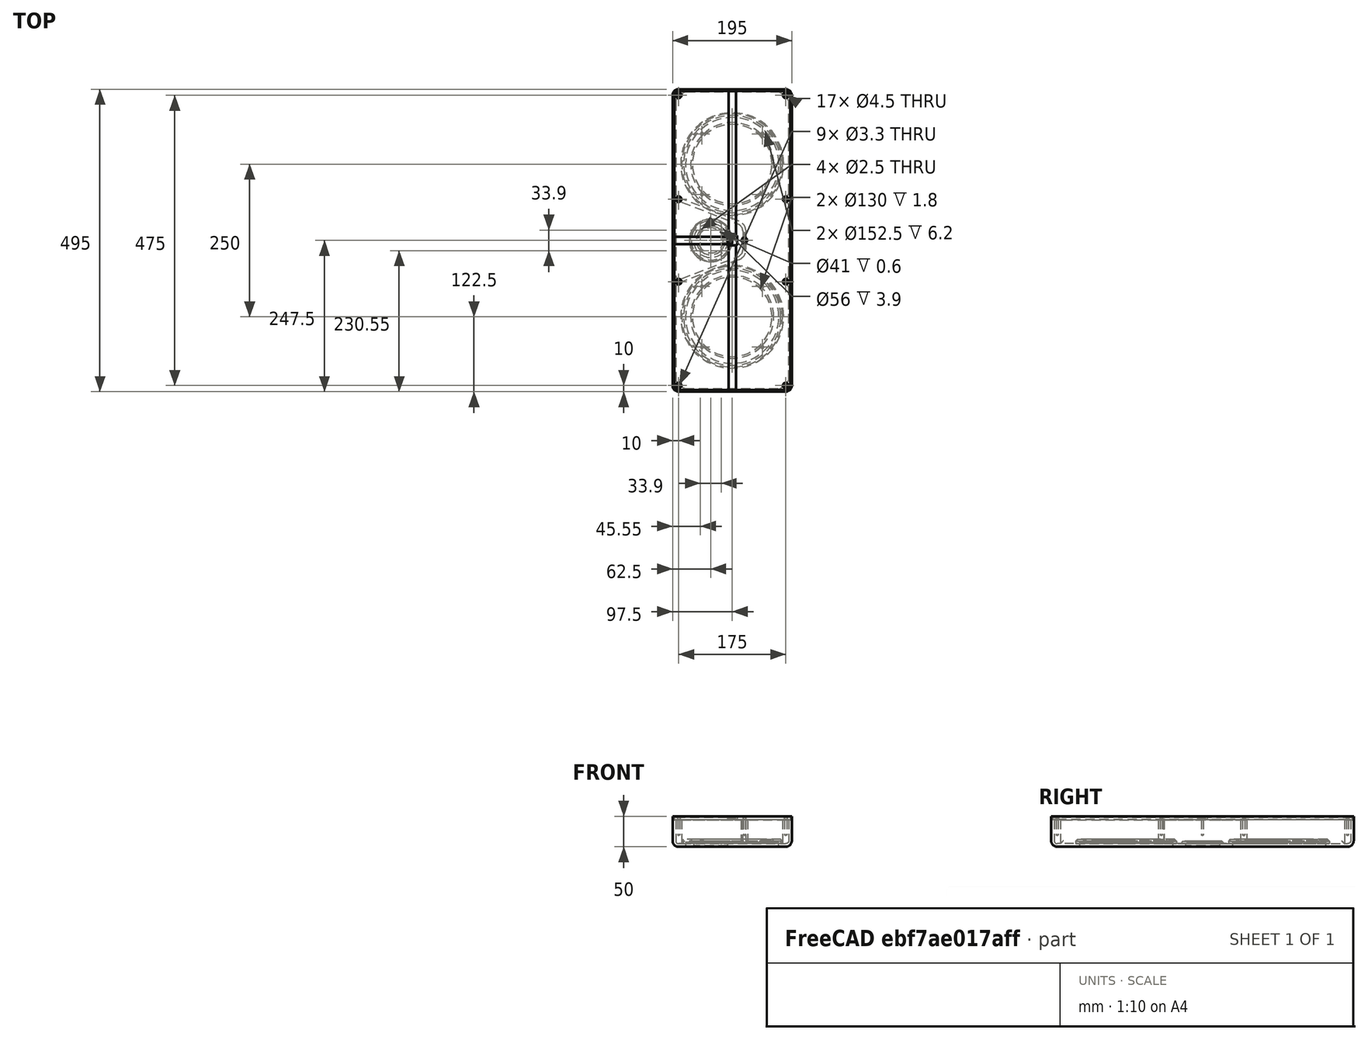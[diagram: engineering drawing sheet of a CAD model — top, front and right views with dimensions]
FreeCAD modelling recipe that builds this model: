
FCSTD DOCUMENT  (FreeCAD 1.1R20260325 (Git shallow))
Label: wallspeakers prototype v6.2
License: All rights reserved
LicenseURL: http://en.wikipedia.org/wiki/All_rights_reserved
objects: TechDraw::DrawViewDimension×43, Sketcher::SketchObject×20, TechDraw::DrawViewAnnotation×7, PartDesign::Pocket×7, PartDesign::Pad×6, TechDraw::DrawProjGroupItem×5, TechDraw::DrawSVGTemplate×4, TechDraw::DrawPage×4, PartDesign::Hole×4, PartDesign::Chamfer×4, App::Point×2, PartDesign::Fillet×2, TechDraw::DrawViewImage×2, Part::Feature×2, PartDesign::Body×2, App::VarSet×1, PartDesign::Thickness×1, App::DocumentObjectGroup×1, Mesh::Feature×1
note: 185 computed .brp shape members not serialized (recipe doc carries the construction recipe); baked Part::Feature solids carry a one-line shape summary decoded from their .brp

FEATURE [Sketcher::SketchObject] Sketch002  label="base geometry"
  ArcFitTolerance = 1e-06
  AttachmentSupport = -> [XY_Plane]
  ExternalTypes = [0]
  FullyConstrained = true
  MakeInternals = false
  MapMode = 5
  _ExternalGeoVersion = 0
  expr: Constraints[3] = <<v>>.bmr_offset
  expr: Constraints[4] = <<v>>.woofer_offset
  expr: Constraints[5] = <<v>>.woofer_offset
  expr: Constraints[6] = <<v>>.ext_height / 2
  expr: Constraints[7] = <<v>>.ext_width / 2
  sketch-geometry (7):
    g0: GeomPoint [constr] X=-97.5 Y=247.5 Z=0
    g1: GeomPoint [constr] X=97.5 Y=247.5 Z=0
    g2: GeomPoint [constr] X=97.5 Y=-247.5 Z=0
    g3: GeomPoint [constr] X=-97.5 Y=-247.5 Z=0
    g4: GeomPoint [constr] X=-35 Y=0 Z=0
    g5: GeomPoint [constr] X=0 Y=125 Z=0
    g6: GeomPoint [constr] X=0 Y=-125 Z=0
  constraints (11):
    c: PointOnObject(g4,g-1)
    c: PointOnObject(g5,g-2)
    c: PointOnObject(g6,g-2)
    c: DistanceX(g4,g-1) = 35
    c: DistanceY(g-1,g5) = 125
    c: DistanceY(g6,g-1) = 125
    c: DistanceY(g-1,g1) = 247.5
    c: DistanceX(g-1,g1) = 97.5
    c: Symmetric(g0,g1,g-2)
    c: Symmetric(g1,g2,g-1)
    c: Symmetric(g3,g2,g-2)
FEATURE [Sketcher::SketchObject] Sketch  label="back panel screw hole geometry"
  ArcFitTolerance = 1e-06
  AttachmentSupport = -> [Sketch002]
  ExternalTypes = [0]
  FullyConstrained = true
  MakeInternals = false
  MapMode = 2
  _ExternalGeoVersion = 0
  expr: Constraints[11] = <<v>>.bmr_enc_offset
  expr: Constraints[1] = <<v>>.ext_height / 2 - <<v>>.screw_inset
  expr: Constraints[2] = <<v>>.ext_width / 2 - <<v>>.screw_inset
  expr: Constraints[8] = <<v>>.ext_width / 2 - <<v>>.screw_inset
  expr: Constraints[9] = <<v>>.bmr_enc_base
  sketch-geometry (9):
    g0: GeomPoint [constr] X=-87.5 Y=237.5 Z=0
    g1: GeomPoint [constr] X=87.5 Y=237.5 Z=0
    g2: GeomPoint [constr] X=87.5 Y=-237.5 Z=0
    g3: GeomPoint [constr] X=-87.5 Y=-237.5 Z=0
    g4: GeomPoint [constr] X=-87.5 Y=-67.5 Z=0
    g5: GeomPoint [constr] X=-87.5 Y=67.5 Z=0
    g6: GeomPoint [constr] X=87.5 Y=67.5 Z=0
    g7: GeomPoint [constr] X=87.5 Y=-67.5 Z=0
    g8: GeomPoint [constr] X=20 Y=0 Z=0
  constraints (12):
    c: PointOnObject(g8,g-1)
    c: DistanceY(g-1,g0) = 237.5
    c: DistanceX(g0,g-1) = 87.5
    c: Symmetric(g0,g1,g-2)
    c: Symmetric(g5,g6,g-2)
    c: Symmetric(g4,g7,g-2)
    c: Symmetric(g3,g2,g-2)
    c: Symmetric(g2,g1,g-1)
    c: DistanceX(g5,g-1) = 87.5
    c: DistanceY(g4,g5) = 135
    c: Symmetric(g5,g4,g-1)
    c: DistanceX(g-1,g8) = 20
FEATURE [App::VarSet] VarSet001  label="v"
  backplate_height = 489.8
  backplate_rebate = 5.9
  backplate_thickness = 5
  backplate_width = 189.8
  bmr_chamfer_depth = 1.5
  bmr_chamfer_width = 6
  bmr_enc_base = 135
  bmr_enc_offset = 20
  bmr_enc_top = 50
  bmr_hole_dia = 41
  bmr_offset = 35
  bmr_plate_thickness = 3
  bmr_rebate_depth = 5.4
  bmr_rebate_dia = 56
  bmr_support_dia = 70
  bmr_support_thickness = 3
  ext_depth = 50
  ext_height = 495
  ext_roundover = 10
  ext_wall = 5
  ext_width = 195
  gasket_thickness = 0.9
  int_depth = 39.1
  rim_width = 2.5
  screw_inset = 10
  screw_post_diameter = 10
  woofer_chamfer_depth = 1
  woofer_chamfer_width = 8
  woofer_cutout_dia = 130
  woofer_offset = 125
  woofer_plate_thickness = 5.3
  woofer_rebate_depth = 7.2
  woofer_rebate_dia = 152.5
  woofer_support_dia = 165
  woofer_support_thickness = 6
  expr: backplate_height = ext_height - rim_width * 2 - 0.2 mm
  expr: backplate_rebate = ext_wall + gasket_thickness
  expr: backplate_width = ext_width - rim_width * 2 - 0.2 mm
  expr: bmr_rebate_depth = bmr_plate_thickness + bmr_chamfer_depth + gasket_thickness
  expr: int_depth = ext_depth - ext_wall - backplate_rebate
  expr: woofer_rebate_depth = woofer_plate_thickness + gasket_thickness + woofer_chamfer_depth
FEATURE [App::Point] Origin001
  Role = Origin
FEATURE [Sketcher::SketchObject] Sketch003  label="main body"
  ArcFitTolerance = 1e-06
  AttachmentSupport = -> [Sketch002]
  ExternalTypes = [0]
  FullyConstrained = true
  MakeInternals = false
  MapMode = 2
  _ExternalGeoVersion = 0
  expr: Constraints[32] = <<v>>.ext_roundover
  expr: Constraints[3] = Sketch002.Constraints[3]
  expr: Constraints[4] = Sketch002.Constraints[4]
  expr: Constraints[5] = Sketch002.Constraints[5]
  expr: Constraints[6] = Sketch002.Constraints[6]
  expr: Constraints[7] = Sketch002.Constraints[7]
  sketch-geometry (17):
    g0: GeomPoint [constr] X=-97.5 Y=247.5 Z=0
    g1: GeomPoint [constr] X=97.5 Y=247.5 Z=0
    g2: GeomPoint [constr] X=97.5 Y=-247.5 Z=0
    g3: GeomPoint [constr] X=-97.5 Y=-247.5 Z=0
    g4: GeomPoint [constr] X=-35 Y=0 Z=0
    g5: GeomPoint [constr] X=0 Y=125 Z=0
    g6: GeomPoint [constr] X=0 Y=-125 Z=0
    g7: LineSegment StartX=-97.5 StartY=237.5 StartZ=0 EndX=-97.5 EndY=-237.5 EndZ=0
    g8: LineSegment StartX=-87.5 StartY=-247.5 StartZ=0 EndX=87.5 EndY=-247.5 EndZ=0
    g9: LineSegment StartX=97.5 StartY=-237.5 StartZ=0 EndX=97.5 EndY=237.5 EndZ=0
    g10: LineSegment StartX=87.5 StartY=247.5 StartZ=0 EndX=-87.5 EndY=247.5 EndZ=0
    g11: ArcOfCircle CenterX=-87.5 CenterY=237.5 CenterZ=0 NormalX=0 NormalY=0 NormalZ=1 AngleXU=0 Radius=10 StartAngle=1.5708 EndAngle=3.14159
    g12: ArcOfCircle CenterX=-87.5 CenterY=-237.5 CenterZ=0 NormalX=0 NormalY=0 NormalZ=1 AngleXU=0 Radius=10 StartAngle=3.14159 EndAngle=4.71239
    g13: ArcOfCircle CenterX=87.5 CenterY=-237.5 CenterZ=0 NormalX=0 NormalY=0 NormalZ=1 AngleXU=0 Radius=10 StartAngle=4.71239 EndAngle=6.28319
    g14: ArcOfCircle CenterX=87.5 CenterY=237.5 CenterZ=0 NormalX=0 NormalY=0 NormalZ=1 AngleXU=0 Radius=10 StartAngle=-3.2e-14 EndAngle=1.5708
    g15: GeomPoint [constr] X=-97.5 Y=247.5 Z=0
    g16: GeomPoint [constr] X=97.5 Y=-247.5 Z=0
  constraints (33):
    c: PointOnObject(g4,g-1)
    c: PointOnObject(g5,g-2)
    c: PointOnObject(g6,g-2)
    c: DistanceX(g4,g-1) = 35
    c: DistanceY(g-1,g5) = 125
    c: DistanceY(g6,g-1) = 125
    c: DistanceY(g-1,g1) = 247.5
    c: DistanceX(g-1,g1) = 97.5
    c: Symmetric(g0,g1,g-2)
    c: Symmetric(g1,g2,g-1)
    c: Symmetric(g3,g2,g-2)
    c: Tangent(g7,g11) = -1.5708
    c: Tangent(g7,g12) = -1.5708
    c: Tangent(g8,g12) = -1.5708
    c: Tangent(g8,g13) = -1.5708
    c: Tangent(g9,g13) = -1.5708
    c: Tangent(g9,g14) = -1.5708
    c: Tangent(g10,g14) = -1.5708
    c: Tangent(g10,g11) = -1.5708
    c: Vertical(g7)
    c: Vertical(g9)
    c: Horizontal(g8)
    c: Horizontal(g10)
    c: Equal(g11,g12)
    c: Equal(g12,g13)
    c: Equal(g13,g14)
    c: PointOnObject(g15,g7)
    c: PointOnObject(g15,g10)
    c: PointOnObject(g16,g8)
    c: PointOnObject(g16,g9)
    c: Coincident(g15,g0)
    c: Coincident(g16,g2)
    c: Radius(g11) = 10
FEATURE [PartDesign::Pad] Pad  label="main body pad"
  Direction = (0,0,1)
  Length = 50
  Length2 = 10
  Profile = -> Sketch003
  ReferenceAxis = -> Sketch003 [N_Axis]
  SideType = 0
  Suppressed = false
  Type = 0
  Type2 = 0
  expr: Length = <<v>>.ext_depth
FEATURE [PartDesign::Fillet] Fillet  label="main body front roundovers"
  Base = -> Pad [Face9]
  BaseFeature = -> Pad
  Radius = 10
  SupportTransform = false
  Suppressed = false
  UseAllEdges = false
  expr: Radius = <<v>>.ext_roundover
FEATURE [Sketcher::SketchObject] Sketch004  label="screw posts layout"
  ArcFitTolerance = 1e-06
  AttachmentSupport = -> [Fillet]
  ExternalTypes = [0]
  FullyConstrained = false
  MakeInternals = false
  MapMode = 5
  Placement = pos=(0,0,50) rot=(0,0,1;0rad)
  _ExternalGeoVersion = 0
  expr: Constraints[117] = <<v>>.screw_post_diameter
  expr: Constraints[11] = Sketch.Constraints[11]
  expr: Constraints[1] = Sketch.Constraints[1]
  expr: Constraints[2] = Sketch.Constraints[2]
  expr: Constraints[81] = <<v>>.ext_height - <<v>>.ext_wall * 2
  expr: Constraints[88] = <<v>>.ext_width - <<v>>.ext_wall * 2
  expr: Constraints[8] = Sketch.Constraints[8]
  expr: Constraints[91] = <<v>>.ext_width - <<v>>.ext_wall * 2
  expr: Constraints[92] = <<v>>.ext_width - <<v>>.ext_wall * 2
  expr: Constraints[9] = Sketch.Constraints[9]
  sketch-geometry (62):
    g0: GeomPoint [constr] X=-87.5 Y=237.5 Z=0
    g1: GeomPoint [constr] X=87.5 Y=237.5 Z=0
    g2: GeomPoint [constr] X=87.5 Y=-237.5 Z=0
    g3: GeomPoint [constr] X=-87.5 Y=-237.5 Z=0
    g4: GeomPoint [constr] X=-87.5 Y=-67.5 Z=0
    g5: GeomPoint [constr] X=-87.5 Y=67.5 Z=0
    g6: GeomPoint [constr] X=87.5 Y=67.5 Z=0
    g7: GeomPoint [constr] X=87.5 Y=-67.5 Z=0
    g8: GeomPoint [constr] X=20 Y=0 Z=0
    g9: LineSegment StartX=-92.5 StartY=-227.5 StartZ=0 EndX=-92.5 EndY=-77.5 EndZ=0
    g10: ArcOfCircle CenterX=-87.5 CenterY=67.5 CenterZ=0 NormalX=0 NormalY=0 NormalZ=1 AngleXU=0 Radius=5 StartAngle=4.71239 EndAngle=7.85398
    g11: ArcOfCircle CenterX=-87.5 CenterY=77.5 CenterZ=0 NormalX=0 NormalY=0 NormalZ=1 AngleXU=0 Radius=5 StartAngle=3.14159 EndAngle=4.71239
    g12: ArcOfCircle CenterX=-87.5 CenterY=57.5 CenterZ=0 NormalX=0 NormalY=0 NormalZ=1 AngleXU=0 Radius=5 StartAngle=1.5708 EndAngle=3.14159
    g13: LineSegment StartX=-92.5 StartY=77.5 StartZ=0 EndX=-92.5 EndY=227.5 EndZ=0
    g14: ArcOfCircle CenterX=-87.5 CenterY=-237.5 CenterZ=0 NormalX=0 NormalY=0 NormalZ=1 AngleXU=0 Radius=5 StartAngle=6.6e-15 EndAngle=1.5708
    g15: ArcOfCircle CenterX=-87.5 CenterY=-227.5 CenterZ=0 NormalX=0 NormalY=0 NormalZ=1 AngleXU=0 Radius=5 StartAngle=3.14159 EndAngle=4.71239
    g16: ArcOfCircle CenterX=-77.5 CenterY=-237.5 CenterZ=0 NormalX=0 NormalY=0 NormalZ=1 AngleXU=0 Radius=5 StartAngle=3.14159 EndAngle=4.71239
    g17: ArcOfCircle CenterX=-87.5 CenterY=-67.5 CenterZ=0 NormalX=0 NormalY=0 NormalZ=1 AngleXU=0 Radius=5 StartAngle=4.71239 EndAngle=7.85398
    g18: ArcOfCircle CenterX=-87.5 CenterY=-57.5 CenterZ=0 NormalX=0 NormalY=0 NormalZ=1 AngleXU=0 Radius=5 StartAngle=3.14159 EndAngle=4.71239
    g19: ArcOfCircle CenterX=-87.5 CenterY=-77.5 CenterZ=0 NormalX=0 NormalY=0 NormalZ=1 AngleXU=0 Radius=5 StartAngle=1.5708 EndAngle=3.14159
    g20: LineSegment StartX=-92.5 StartY=-57.5 StartZ=0 EndX=-92.5 EndY=57.5 EndZ=0
    g21: ArcOfCircle CenterX=-87.5 CenterY=237.5 CenterZ=0 NormalX=0 NormalY=0 NormalZ=1 AngleXU=0 Radius=5 StartAngle=4.71239 EndAngle=6.28319
    g22: ArcOfCircle CenterX=-77.5 CenterY=237.5 CenterZ=0 NormalX=0 NormalY=0 NormalZ=1 AngleXU=0 Radius=5 StartAngle=1.5708 EndAngle=3.14159
    g23: ArcOfCircle CenterX=-87.5 CenterY=227.5 CenterZ=0 NormalX=0 NormalY=0 NormalZ=1 AngleXU=0 Radius=5 StartAngle=1.5708 EndAngle=3.14159
    g24: GeomPoint [constr] X=87.5 Y=237.5 Z=0
    g25: GeomPoint [constr] X=-87.5 Y=237.5 Z=0
    g26: GeomPoint [constr] X=-87.5 Y=-237.5 Z=0
    g27: GeomPoint [constr] X=87.5 Y=-237.5 Z=0
    g28: GeomPoint [constr] X=87.5 Y=-67.5 Z=0
    g29: GeomPoint [constr] X=87.5 Y=67.5 Z=0
    g30: GeomPoint [constr] X=-87.5 Y=67.5 Z=0
    g31: GeomPoint [constr] X=-87.5 Y=-67.5 Z=0
    g32: GeomPoint [constr] X=-20 Y=0 Z=0
    g33: LineSegment StartX=92.5 StartY=-227.5 StartZ=0 EndX=92.5 EndY=-77.5 EndZ=0
    g34: ArcOfCircle CenterX=87.5 CenterY=67.5 CenterZ=0 NormalX=0 NormalY=0 NormalZ=1 AngleXU=0 Radius=5 StartAngle=1.5708 EndAngle=4.71239
    g35: ArcOfCircle CenterX=87.5 CenterY=77.5 CenterZ=0 NormalX=0 NormalY=0 NormalZ=1 AngleXU=0 Radius=5 StartAngle=4.71239 EndAngle=6.28319
    g36: ArcOfCircle CenterX=87.5 CenterY=57.5 CenterZ=0 NormalX=0 NormalY=0 NormalZ=1 AngleXU=0 Radius=5 StartAngle=0 EndAngle=1.5708
    g37: LineSegment StartX=92.5 StartY=77.5 StartZ=0 EndX=92.5 EndY=227.5 EndZ=0
    g38: ArcOfCircle CenterX=87.5 CenterY=-237.5 CenterZ=0 NormalX=0 NormalY=0 NormalZ=1 AngleXU=0 Radius=5 StartAngle=1.5708 EndAngle=3.14159
    g39: ArcOfCircle CenterX=87.5 CenterY=-227.5 CenterZ=0 NormalX=0 NormalY=0 NormalZ=1 AngleXU=0 Radius=5 StartAngle=4.71239 EndAngle=6.28319
    g40: ArcOfCircle CenterX=77.5 CenterY=-237.5 CenterZ=0 NormalX=0 NormalY=0 NormalZ=1 AngleXU=0 Radius=5 StartAngle=4.71239 EndAngle=6.28319
    g41: ArcOfCircle CenterX=87.5 CenterY=-67.5 CenterZ=0 NormalX=0 NormalY=0 NormalZ=1 AngleXU=0 Radius=5 StartAngle=1.5708 EndAngle=4.71239
    g42: ArcOfCircle CenterX=87.5 CenterY=-57.5 CenterZ=0 NormalX=0 NormalY=0 NormalZ=1 AngleXU=0 Radius=5 StartAngle=4.71239 EndAngle=6.28319
    g43: ArcOfCircle CenterX=87.5 CenterY=-77.5 CenterZ=0 NormalX=0 NormalY=0 NormalZ=1 AngleXU=0 Radius=5 StartAngle=-9e-16 EndAngle=1.5708
    g44: LineSegment StartX=92.5 StartY=-57.5 StartZ=0 EndX=92.5 EndY=57.5 EndZ=0
    g45: ArcOfCircle CenterX=87.5 CenterY=237.5 CenterZ=0 NormalX=0 NormalY=0 NormalZ=1 AngleXU=0 Radius=5 StartAngle=3.14159 EndAngle=4.71239
    g46: ArcOfCircle CenterX=77.5 CenterY=237.5 CenterZ=0 NormalX=0 NormalY=0 NormalZ=1 AngleXU=0 Radius=5 StartAngle=-4.4e-15 EndAngle=1.5708
    g47: ArcOfCircle CenterX=87.5 CenterY=227.5 CenterZ=0 NormalX=0 NormalY=0 NormalZ=1 AngleXU=0 Radius=5 StartAngle=8e-16 EndAngle=1.5708
    g48: LineSegment StartX=-77.5 StartY=242.5 StartZ=0 EndX=77.5 EndY=242.5 EndZ=0
    g49: LineSegment StartX=-77.5 StartY=-242.5 StartZ=0 EndX=77.5 EndY=-242.5 EndZ=0
    g50: LineSegment [constr] StartX=-87.5 StartY=232.5 StartZ=0 EndX=-82.5 EndY=237.5 EndZ=0
    g51: LineSegment StartX=-95 StartY=235 StartZ=0 EndX=-95 EndY=-235 EndZ=0
    g52: LineSegment StartX=-85 StartY=-245 StartZ=0 EndX=85 EndY=-245 EndZ=0
    g53: LineSegment StartX=95 StartY=-235 StartZ=0 EndX=95 EndY=235 EndZ=0
    g54: LineSegment StartX=85 StartY=245 StartZ=0 EndX=-85 EndY=245 EndZ=0
    g55: ArcOfCircle CenterX=-85 CenterY=235 CenterZ=0 NormalX=0 NormalY=0 NormalZ=1 AngleXU=0 Radius=10 StartAngle=1.5708 EndAngle=3.14159
    g56: ArcOfCircle CenterX=-85 CenterY=-235 CenterZ=0 NormalX=0 NormalY=0 NormalZ=1 AngleXU=0 Radius=10 StartAngle=3.14159 EndAngle=4.71239
    g57: ArcOfCircle CenterX=85 CenterY=-235 CenterZ=0 NormalX=0 NormalY=0 NormalZ=1 AngleXU=0 Radius=10 StartAngle=4.71239 EndAngle=6.28319
    g58: ArcOfCircle CenterX=85 CenterY=235 CenterZ=0 NormalX=0 NormalY=0 NormalZ=1 AngleXU=0 Radius=10 StartAngle=1.04e-14 EndAngle=1.5708
    g59: GeomPoint [constr] X=-95 Y=245 Z=0
    g60: GeomPoint [constr] X=95 Y=-245 Z=0
    g61: Circle CenterX=20 CenterY=0 CenterZ=0 NormalX=0 NormalY=0 NormalZ=1 AngleXU=0 Radius=5
  constraints (118):
    c: PointOnObject(g8,g-1)
    c: DistanceY(g-1,g0) = 237.5
    c: DistanceX(g0,g-1) = 87.5
    c: Symmetric(g0,g1,g-2)
    c: Symmetric(g5,g6,g-2)
    c: Symmetric(g4,g7,g-2)
    c: Symmetric(g3,g2,g-2)
    c: Symmetric(g2,g1,g-1)
    c: DistanceX(g5,g-1) = 87.5
    c: DistanceY(g4,g5) = 135
    c: Symmetric(g5,g4,g-1)
    c: DistanceX(g-1,g8) = 20
    c: Radius(g10) = 5
    c: Equal(g11,g10)
    c: Equal(g12,g10)
    c: Tangent(g11,g10) = 1.5708
    c: Tangent(g12,g10) = 1.5708
    c: Tangent(g13,g11) = 1.5708
    c: Radius(g14) = 5
    c: Equal(g15,g14)
    c: Equal(g16,g14)
    c: Tangent(g15,g14) = 1.5708
    c: Tangent(g16,g14) = 1.5708
    c: Radius(g17) = 5
    c: Equal(g18,g17)
    c: Equal(g19,g17)
    c: Tangent(g18,g17) = 1.5708
    c: Tangent(g19,g17) = 1.5708
    c: Tangent(g20,g18) = 1.5708
    c: Vertical(g20)
    c: Vertical(g9)
    c: Coincident(g17,g4)
    c: Coincident(g14,g3)
    c: Tangent(g15,g9) = 1.5708
    c: Coincident(g10,g5)
    c: Tangent(g12,g20) = 1.5708
    c: Radius(g21) = 5
    c: Equal(g22,g21)
    c: Equal(g23,g21)
    c: Tangent(g22,g21) = 1.5708
    c: Tangent(g23,g21) = 1.5708
    c: Tangent(g23,g13) = 1.5708
    c: Coincident(g21,g0)
    c: Symmetric(g11,g19,g-1)
    c: Tangent(g9,g19) = 1.5708
    c: Radius(g34) = 5
    c: Equal(g35,g34)
    c: Equal(g36,g34)
    c: Tangent(g35,g34) = 1.5708
    c: Tangent(g36,g34) = 1.5708
    c: Tangent(g37,g35) = -1.5708
    c: Radius(g38) = 5
    c: Equal(g39,g38)
    c: Equal(g40,g38)
    c: Tangent(g39,g38) = 1.5708
    c: Tangent(g40,g38) = 1.5708
    c: Radius(g41) = 5
    c: Equal(g42,g41)
    c: Equal(g43,g41)
    c: Tangent(g42,g41) = 1.5708
    c: Tangent(g43,g41) = 1.5708
    c: Tangent(g44,g42) = -1.5708
    c: Vertical(g33)
    c: Coincident(g41,g28)
    c: Coincident(g38,g27)
    c: Tangent(g39,g33) = -1.5708
    c: Coincident(g34,g29)
    c: Tangent(g36,g44) = -1.5708
    c: Radius(g45) = 5
    c: Equal(g47,g45)
    c: Tangent(g46,g45) = 1.5708
    c: Tangent(g47,g45) = 1.5708
    c: Tangent(g47,g37) = -1.5708
    c: Coincident(g45,g24)
    c: Tangent(g33,g43) = -1.5708
    c: Symmetric(g46,g22,g-2)
    c: Tangent(g48,g46) = 1.5708
    c: Tangent(g48,g22) = 1.5708
    c: Tangent(g49,g16) = -1.5708
    c: Horizontal(g49)
    c: Tangent(g49,g40) = -1.5708
    c: Distance(g49,g48) = 485
    c: Coincident(g28,g7)
    c: Coincident(g29,g6)
    c: Coincident(g24,g1)
    c: Coincident(g27,g2)
    c: Coincident(g50,g21)
    c: Coincident(g50,g21)
    c: Distance(g44,g20) = 185
    c: Symmetric(g13,g37,g-2)
    c: Symmetric(g12,g36,g-2)
    c: DistanceX(g11,g35) = 185
    c: Distance(g33,g9) = 185
    c: Angle(g50) = 0.785398
    c: Tangent(g51,g55) = -1.5708
    c: Tangent(g51,g56) = -1.5708
    c: Tangent(g52,g56) = -1.5708
    c: Tangent(g52,g57) = -1.5708
    c: Tangent(g53,g57) = -1.5708
    c: Tangent(g53,g58) = -1.5708
    c: Tangent(g54,g58) = -1.5708
    c: Tangent(g54,g55) = -1.5708
    c: Vertical(g51)
    c: Horizontal(g52)
    c: Horizontal(g54)
    c: Equal(g55,g56)
    c: Equal(g57,g58)
    c: PointOnObject(g59,g51)
    c: PointOnObject(g59,g54)
    c: PointOnObject(g60,g52)
    c: PointOnObject(g60,g53)
    c: Radius(g55) = 10
    c: Distance(g53,g51) = 190
    c: Symmetric(g51,g53,g-2)
    c: Distance(g52,g54) = 490
    c: Symmetric(g53,g53,g-1)
    c: Coincident(g61,g8)
    c: Diameter(g61) = 10
FEATURE [Sketcher::SketchObject] Sketch005  label="woofer rebates"
  ArcFitTolerance = 1e-06
  AttachmentSupport = -> [Origin]
  ExternalTypes = [0]
  FullyConstrained = true
  MakeInternals = false
  MapMode = 5
  _ExternalGeoVersion = 0
  expr: Constraints[12] = VarSet001.woofer_rebate_dia
  expr: Constraints[3] = Sketch002.Constraints[3]
  expr: Constraints[4] = Sketch002.Constraints[4]
  expr: Constraints[5] = Sketch002.Constraints[5]
  expr: Constraints[6] = Sketch002.Constraints[6]
  expr: Constraints[7] = Sketch002.Constraints[7]
  sketch-geometry (9):
    g0: GeomPoint [constr] X=-97.5 Y=247.5 Z=0
    g1: GeomPoint [constr] X=97.5 Y=247.5 Z=0
    g2: GeomPoint [constr] X=97.5 Y=-247.5 Z=0
    g3: GeomPoint [constr] X=-97.5 Y=-247.5 Z=0
    g4: GeomPoint [constr] X=-35 Y=0 Z=0
    g5: GeomPoint [constr] X=0 Y=125 Z=0
    g6: GeomPoint [constr] X=0 Y=-125 Z=0
    g7: Circle CenterX=0 CenterY=125 CenterZ=0 NormalX=0 NormalY=0 NormalZ=1 AngleXU=0 Radius=76.25
    g8: Circle CenterX=0 CenterY=-125 CenterZ=0 NormalX=0 NormalY=0 NormalZ=1 AngleXU=0 Radius=76.25
  constraints (15):
    c: PointOnObject(g4,g-1)
    c: PointOnObject(g5,g-2)
    c: PointOnObject(g6,g-2)
    c: DistanceX(g4,g-1) = 35
    c: DistanceY(g-1,g5) = 125
    c: DistanceY(g6,g-1) = 125
    c: DistanceY(g-1,g1) = 247.5
    c: DistanceX(g-1,g1) = 97.5
    c: Symmetric(g0,g1,g-2)
    c: Symmetric(g1,g2,g-1)
    c: Symmetric(g3,g2,g-2)
    c: Coincident(g8,g6)
    c: Diameter(g7) = 152.5
    c: Equal(g7,g8)
    c: Coincident(g5,g7)
FEATURE [Sketcher::SketchObject] Sketch006
  ArcFitTolerance = 1e-06
  AttachmentOffset = pos=(0,0,5) rot=(0,0,1;0rad)
  AttachmentSupport = -> [Origin]
  ExternalTypes = [0]
  FullyConstrained = true
  MakeInternals = false
  MapMode = 5
  Placement = pos=(0,0,5) rot=(0,0,1;0rad)
  _ExternalGeoVersion = 0
  expr: .AttachmentOffset.Base.z = <<v>>.ext_wall
  expr: Constraints[14] = Sketch002.Constraints[3]
  expr: Constraints[15] = Sketch002.Constraints[4]
  expr: Constraints[16] = Sketch002.Constraints[5]
  expr: Constraints[17] = Sketch002.Constraints[6]
  expr: Constraints[18] = Sketch002.Constraints[7]
  expr: Constraints[22] = VarSet001.woofer_support_dia
  expr: Constraints[3] = Sketch002.Constraints[3]
  expr: Constraints[4] = Sketch002.Constraints[4]
  expr: Constraints[5] = Sketch002.Constraints[5]
  expr: Constraints[6] = Sketch002.Constraints[6]
  expr: Constraints[7] = Sketch002.Constraints[7]
  sketch-geometry (16):
    g0: GeomPoint [constr] X=-97.5 Y=247.5 Z=0
    g1: GeomPoint [constr] X=97.5 Y=247.5 Z=0
    g2: GeomPoint [constr] X=97.5 Y=-247.5 Z=0
    g3: GeomPoint [constr] X=-97.5 Y=-247.5 Z=0
    g4: GeomPoint [constr] X=-35 Y=0 Z=0
    g5: GeomPoint [constr] X=0 Y=125 Z=0
    g6: GeomPoint [constr] X=0 Y=-125 Z=0
    g7: GeomPoint [constr] X=-97.5 Y=247.5 Z=0
    g8: GeomPoint [constr] X=97.5 Y=247.5 Z=0
    g9: GeomPoint [constr] X=97.5 Y=-247.5 Z=0
    g10: GeomPoint [constr] X=-97.5 Y=-247.5 Z=0
    g11: GeomPoint [constr] X=-35 Y=0 Z=0
    g12: GeomPoint [constr] X=0 Y=125 Z=0
    g13: GeomPoint [constr] X=0 Y=-125 Z=0
    g14: Circle CenterX=0 CenterY=125 CenterZ=0 NormalX=0 NormalY=0 NormalZ=1 AngleXU=0 Radius=82.5
    g15: Circle CenterX=0 CenterY=-125 CenterZ=0 NormalX=0 NormalY=0 NormalZ=1 AngleXU=0 Radius=82.5
  constraints (26):
    c: PointOnObject(g4,g-1)
    c: PointOnObject(g5,g-2)
    c: PointOnObject(g6,g-2)
    c: DistanceX(g4,g-1) = 35
    c: DistanceY(g-1,g5) = 125
    c: DistanceY(g6,g-1) = 125
    c: DistanceY(g-1,g1) = 247.5
    c: DistanceX(g-1,g1) = 97.5
    c: Symmetric(g0,g1,g-2)
    c: Symmetric(g1,g2,g-1)
    c: Symmetric(g3,g2,g-2)
    c: PointOnObject(g11,g-1)
    c: PointOnObject(g12,g-2)
    c: PointOnObject(g13,g-2)
    c: DistanceX(g11,g-1) = 35
    c: DistanceY(g-1,g12) = 125
    c: DistanceY(g13,g-1) = 125
    c: DistanceY(g-1,g8) = 247.5
    c: DistanceX(g-1,g8) = 97.5
    c: Symmetric(g7,g8,g-2)
    c: Symmetric(g8,g9,g-1)
    c: Symmetric(g10,g9,g-2)
    c: Diameter(g14) = 165
    c: Coincident(g15,g6)
    c: Equal(g14,g15)
    c: Coincident(g14,g5)
FEATURE [Sketcher::SketchObject] Sketch007
  ArcFitTolerance = 1e-06
  AttachmentSupport = -> [Origin]
  ExternalTypes = [0]
  FullyConstrained = true
  MakeInternals = false
  MapMode = 5
  _ExternalGeoVersion = 0
  expr: Constraints[12] = VarSet001.woofer_cutout_dia
  expr: Constraints[3] = Sketch002.Constraints[3]
  expr: Constraints[4] = Sketch002.Constraints[4]
  expr: Constraints[5] = Sketch002.Constraints[5]
  expr: Constraints[6] = Sketch002.Constraints[6]
  expr: Constraints[7] = Sketch002.Constraints[7]
  sketch-geometry (9):
    g0: GeomPoint [constr] X=-97.5 Y=247.5 Z=0
    g1: GeomPoint [constr] X=97.5 Y=247.5 Z=0
    g2: GeomPoint [constr] X=97.5 Y=-247.5 Z=0
    g3: GeomPoint [constr] X=-97.5 Y=-247.5 Z=0
    g4: GeomPoint [constr] X=-35 Y=0 Z=0
    g5: GeomPoint [constr] X=0 Y=125 Z=0
    g6: GeomPoint [constr] X=0 Y=-125 Z=0
    g7: Circle CenterX=0 CenterY=125 CenterZ=0 NormalX=0 NormalY=0 NormalZ=1 AngleXU=0 Radius=65
    g8: Circle CenterX=0 CenterY=-125 CenterZ=0 NormalX=0 NormalY=0 NormalZ=1 AngleXU=0 Radius=65
  constraints (15):
    c: PointOnObject(g4,g-1)
    c: PointOnObject(g5,g-2)
    c: PointOnObject(g6,g-2)
    c: DistanceX(g4,g-1) = 35
    c: DistanceY(g-1,g5) = 125
    c: DistanceY(g6,g-1) = 125
    c: DistanceY(g-1,g1) = 247.5
    c: DistanceX(g-1,g1) = 97.5
    c: Symmetric(g0,g1,g-2)
    c: Symmetric(g1,g2,g-1)
    c: Symmetric(g3,g2,g-2)
    c: Coincident(g7,g5)
    c: Diameter(g7) = 130
    c: Equal(g7,g8)
    c: Coincident(g8,g6)
FEATURE [Sketcher::SketchObject] Sketch008  label="bmr rebate"
  ArcFitTolerance = 1e-06
  AttachmentSupport = -> [Origin]
  ExternalTypes = [0]
  FullyConstrained = true
  MakeInternals = false
  MapMode = 5
  _ExternalGeoVersion = 0
  expr: Constraints[11] = VarSet001.bmr_rebate_dia
  expr: Constraints[3] = <<v>>.bmr_offset
  expr: Constraints[4] = Sketch002.Constraints[4]
  expr: Constraints[5] = Sketch002.Constraints[5]
  expr: Constraints[6] = Sketch002.Constraints[6]
  expr: Constraints[7] = Sketch002.Constraints[7]
  sketch-geometry (8):
    g0: GeomPoint [constr] X=-97.5 Y=247.5 Z=0
    g1: GeomPoint [constr] X=97.5 Y=247.5 Z=0
    g2: GeomPoint [constr] X=97.5 Y=-247.5 Z=0
    g3: GeomPoint [constr] X=-97.5 Y=-247.5 Z=0
    g4: GeomPoint [constr] X=-35 Y=0 Z=0
    g5: GeomPoint [constr] X=0 Y=125 Z=0
    g6: GeomPoint [constr] X=0 Y=-125 Z=0
    g7: Circle CenterX=-35 CenterY=0 CenterZ=0 NormalX=0 NormalY=0 NormalZ=1 AngleXU=0 Radius=28
  constraints (13):
    c: PointOnObject(g4,g-1)
    c: PointOnObject(g5,g-2)
    c: PointOnObject(g6,g-2)
    c: DistanceX(g4,g-1) = 35
    c: DistanceY(g-1,g5) = 125
    c: DistanceY(g6,g-1) = 125
    c: DistanceY(g-1,g1) = 247.5
    c: DistanceX(g-1,g1) = 97.5
    c: Symmetric(g0,g1,g-2)
    c: Symmetric(g1,g2,g-1)
    c: Symmetric(g3,g2,g-2)
    c: Diameter(g7) = 56
    c: Coincident(g7,g4)
FEATURE [Sketcher::SketchObject] Sketch009  label="bmr_support"
  ArcFitTolerance = 1e-06
  AttachmentOffset = pos=(0,0,5) rot=(0,0,1;0rad)
  AttachmentSupport = -> [Sketch008]
  ExternalTypes = [0]
  FullyConstrained = true
  MakeInternals = false
  MapMode = 2
  Placement = pos=(0,0,5) rot=(0,0,1;0rad)
  _ExternalGeoVersion = 0
  expr: .AttachmentOffset.Base.z = <<v>>.ext_wall
  expr: Constraints[12] = VarSet001.bmr_support_dia
  expr: Constraints[3] = Sketch002.Constraints[3]
  expr: Constraints[4] = Sketch002.Constraints[4]
  expr: Constraints[5] = Sketch002.Constraints[5]
  expr: Constraints[6] = Sketch002.Constraints[6]
  expr: Constraints[7] = Sketch002.Constraints[7]
  sketch-geometry (8):
    g0: GeomPoint [constr] X=-97.5 Y=247.5 Z=0
    g1: GeomPoint [constr] X=97.5 Y=247.5 Z=0
    g2: GeomPoint [constr] X=97.5 Y=-247.5 Z=0
    g3: GeomPoint [constr] X=-97.5 Y=-247.5 Z=0
    g4: GeomPoint [constr] X=-35 Y=0 Z=0
    g5: GeomPoint [constr] X=0 Y=125 Z=0
    g6: GeomPoint [constr] X=0 Y=-125 Z=0
    g7: Circle CenterX=-35 CenterY=0 CenterZ=0 NormalX=0 NormalY=0 NormalZ=1 AngleXU=0 Radius=35
  constraints (13):
    c: PointOnObject(g4,g-1)
    c: PointOnObject(g5,g-2)
    c: PointOnObject(g6,g-2)
    c: DistanceX(g4,g-1) = 35
    c: DistanceY(g-1,g5) = 125
    c: DistanceY(g6,g-1) = 125
    c: DistanceY(g-1,g1) = 247.5
    c: DistanceX(g-1,g1) = 97.5
    c: Symmetric(g0,g1,g-2)
    c: Symmetric(g1,g2,g-1)
    c: Symmetric(g3,g2,g-2)
    c: Coincident(g7,g4)
    c: Diameter(g7) = 70
FEATURE [Sketcher::SketchObject] Sketch010
  ArcFitTolerance = 1e-06
  AttachmentSupport = -> [Origin]
  ExternalTypes = [0]
  FullyConstrained = true
  MakeInternals = false
  MapMode = 5
  _ExternalGeoVersion = 0
  expr: Constraints[12] = <<v>>.bmr_hole_dia
  expr: Constraints[3] = <<v>>.bmr_offset
  expr: Constraints[4] = Sketch002.Constraints[4]
  expr: Constraints[5] = Sketch002.Constraints[5]
  expr: Constraints[6] = Sketch002.Constraints[6]
  expr: Constraints[7] = Sketch002.Constraints[7]
  sketch-geometry (8):
    g0: GeomPoint [constr] X=-97.5 Y=247.5 Z=0
    g1: GeomPoint [constr] X=97.5 Y=247.5 Z=0
    g2: GeomPoint [constr] X=97.5 Y=-247.5 Z=0
    g3: GeomPoint [constr] X=-97.5 Y=-247.5 Z=0
    g4: GeomPoint [constr] X=-35 Y=0 Z=0
    g5: GeomPoint [constr] X=0 Y=125 Z=0
    g6: GeomPoint [constr] X=0 Y=-125 Z=0
    g7: Circle CenterX=-35 CenterY=0 CenterZ=0 NormalX=0 NormalY=0 NormalZ=1 AngleXU=0 Radius=20.5
  constraints (13):
    c: PointOnObject(g4,g-1)
    c: PointOnObject(g5,g-2)
    c: PointOnObject(g6,g-2)
    c: DistanceX(g4,g-1) = 35
    c: DistanceY(g-1,g5) = 125
    c: DistanceY(g6,g-1) = 125
    c: DistanceY(g-1,g1) = 247.5
    c: DistanceX(g-1,g1) = 97.5
    c: Symmetric(g0,g1,g-2)
    c: Symmetric(g1,g2,g-1)
    c: Symmetric(g3,g2,g-2)
    c: Coincident(g7,g4)
    c: Diameter(g7) = 41
FEATURE [Sketcher::SketchObject] Sketch011  label="woofer screw hole layout"
  ArcFitTolerance = 1e-06
  AttachmentOffset = pos=(0,0,7.2) rot=(0,0,1;0rad)
  AttachmentSupport = -> [Origin]
  ExternalTypes = [0]
  FullyConstrained = true
  MakeInternals = false
  MapMode = 5
  Placement = pos=(0,0,7.2) rot=(0,0,1;0rad)
  _ExternalGeoVersion = 0
  expr: .AttachmentOffset.Base.z = <<v>>.woofer_rebate_depth
  expr: Constraints[4] = <<v>>.woofer_offset
  expr: Constraints[5] = <<v>>.woofer_offset
  sketch-geometry (10):
    g0: GeomPoint X=-49.53 Y=174.53 Z=0
    g1: GeomPoint X=49.53 Y=174.53 Z=0
    g2: GeomPoint X=49.53 Y=75.47 Z=0
    g3: GeomPoint X=-49.53 Y=75.47 Z=0
    g4: GeomPoint X=49.53 Y=-75.47 Z=0
    g5: GeomPoint X=-49.53 Y=-75.47 Z=0
    g6: GeomPoint X=-49.53 Y=-174.53 Z=0
    g7: GeomPoint X=49.53 Y=-174.53 Z=0
    g8: LineSegment [constr] StartX=100 StartY=-125 StartZ=0 EndX=-100 EndY=-125 EndZ=0
    g9: LineSegment [constr] StartX=100 StartY=125 StartZ=0 EndX=-100 EndY=125 EndZ=0
  constraints (16):
    c: DistanceX(g9,g9) = 200
    c: DistanceX(g8,g8) = 200
    c: Symmetric(g9,g9,g-2)
    c: Symmetric(g8,g8,g-2)
    c: Distance(g-1,g9) = 125
    c: Distance(g-1,g8) = 125
    c: Distance(g1,g9) = 49.53
    c: DistanceX(g-1,g1) = 49.53
    c: Symmetric(g1,g0,g-2)
    c: Symmetric(g0,g3,g9)
    c: Symmetric(g1,g2,g9)
    c: Distance(g4,g8) = 49.53
    c: Distance(g4,g-2) = 49.53
    c: Symmetric(g4,g5,g-2)
    c: Symmetric(g5,g6,g8)
    c: Symmetric(g4,g7,g8)
FEATURE [Sketcher::SketchObject] Sketch012  label="bmr screw hole layout"
  ArcFitTolerance = 1e-06
  AttachmentOffset = pos=(0,0,5.4) rot=(0,0,1;0rad)
  AttachmentSupport = -> [Origin]
  ExternalTypes = [0]
  FullyConstrained = true
  MakeInternals = false
  MapMode = 5
  Placement = pos=(0,0,5.4) rot=(0,0,1;0rad)
  _ExternalGeoVersion = 0
  expr: .AttachmentOffset.Base.z = <<v>>.bmr_rebate_depth
  expr: Constraints[0] = <<v>>.bmr_offset
  sketch-geometry (5):
    g0: LineSegment [constr] StartX=-35 StartY=50 StartZ=0 EndX=-35 EndY=-50 EndZ=0
    g1: GeomPoint X=-51.95 Y=16.95 Z=0
    g2: GeomPoint X=-18.05 Y=16.95 Z=0
    g3: GeomPoint X=-18.05 Y=-16.95 Z=0
    g4: GeomPoint X=-51.95 Y=-16.95 Z=0
  constraints (8):
    c: Distance(g-2,g0) = 35
    c: DistanceY(g0,g0) = 100
    c: Symmetric(g0,g0,g-1)
    c: Distance(g1,g-1) = 16.95
    c: Distance(g1,g0) = 16.95
    c: Symmetric(g1,g2,g0)
    c: Symmetric(g1,g4,g-1)
    c: Symmetric(g2,g3,g-1)
FEATURE [Sketcher::SketchObject] Sketch013  label="post screw hole layout"
  ArcFitTolerance = 1e-06
  AttachmentOffset = pos=(0,0,44.1) rot=(0,0,1;0rad)
  AttachmentSupport = -> [Origin]
  ExternalTypes = [0]
  FullyConstrained = true
  MakeInternals = false
  MapMode = 5
  Placement = pos=(0,0,44.1) rot=(0,0,1;0rad)
  _ExternalGeoVersion = 0
  expr: .AttachmentOffset.Base.z = <<v>>.int_depth + <<v>>.ext_wall
  expr: Constraints[11] = Sketch.Constraints[11]
  expr: Constraints[1] = Sketch.Constraints[1]
  expr: Constraints[2] = Sketch.Constraints[2]
  expr: Constraints[8] = Sketch.Constraints[8]
  expr: Constraints[9] = Sketch.Constraints[9]
  sketch-geometry (9):
    g0: GeomPoint X=-87.5 Y=237.5 Z=0
    g1: GeomPoint X=87.5 Y=237.5 Z=0
    g2: GeomPoint X=87.5 Y=-237.5 Z=0
    g3: GeomPoint X=-87.5 Y=-237.5 Z=0
    g4: GeomPoint X=-87.5 Y=-67.5 Z=0
    g5: GeomPoint X=-87.5 Y=67.5 Z=0
    g6: GeomPoint X=87.5 Y=67.5 Z=0
    g7: GeomPoint X=87.5 Y=-67.5 Z=0
    g8: GeomPoint X=20 Y=0 Z=0
  constraints (12):
    c: PointOnObject(g8,g-1)
    c: DistanceY(g-1,g0) = 237.5
    c: DistanceX(g0,g-1) = 87.5
    c: Symmetric(g0,g1,g-2)
    c: Symmetric(g5,g6,g-2)
    c: Symmetric(g4,g7,g-2)
    c: Symmetric(g3,g2,g-2)
    c: Symmetric(g2,g1,g-1)
    c: DistanceX(g5,g-1) = 87.5
    c: DistanceY(g4,g5) = 135
    c: Symmetric(g5,g4,g-1)
    c: DistanceX(g-1,g8) = 20
FEATURE [Sketcher::SketchObject] Sketch014  label="rim pocket outline"
  ArcFitTolerance = 1e-06
  AttachmentOffset = pos=(0,0,50) rot=(0,0,1;0rad)
  AttachmentSupport = -> [Origin]
  ExternalTypes = [0]
  FullyConstrained = true
  MakeInternals = false
  MapMode = 5
  Placement = pos=(0,0,50) rot=(0,0,1;0rad)
  _ExternalGeoVersion = 0
  expr: .AttachmentOffset.Base.z = <<v>>.ext_depth
  expr: Constraints[17] = <<v>>.ext_roundover - <<v>>.rim_width
  expr: Constraints[18] = <<v>>.ext_width - <<v>>.rim_width * 2
  expr: Constraints[19] = <<v>>.ext_height - <<v>>.rim_width * 2
  sketch-geometry (10):
    g0: LineSegment StartX=-95 StartY=237.5 StartZ=0 EndX=-95 EndY=-237.5 EndZ=0
    g1: LineSegment StartX=-87.5 StartY=-245 StartZ=0 EndX=87.5 EndY=-245 EndZ=0
    g2: LineSegment StartX=95 StartY=-237.5 StartZ=0 EndX=95 EndY=237.5 EndZ=0
    g3: LineSegment StartX=87.5 StartY=245 StartZ=0 EndX=-87.5 EndY=245 EndZ=0
    g4: ArcOfCircle CenterX=-87.5 CenterY=237.5 CenterZ=0 NormalX=0 NormalY=0 NormalZ=1 AngleXU=0 Radius=7.5 StartAngle=1.5708 EndAngle=3.14159
    g5: ArcOfCircle CenterX=-87.5 CenterY=-237.5 CenterZ=0 NormalX=0 NormalY=0 NormalZ=1 AngleXU=0 Radius=7.5 StartAngle=3.14159 EndAngle=4.71239
    g6: ArcOfCircle CenterX=87.5 CenterY=-237.5 CenterZ=0 NormalX=0 NormalY=0 NormalZ=1 AngleXU=0 Radius=7.5 StartAngle=4.71239 EndAngle=6.28319
    g7: ArcOfCircle CenterX=87.5 CenterY=237.5 CenterZ=0 NormalX=0 NormalY=0 NormalZ=1 AngleXU=0 Radius=7.5 StartAngle=1.6e-15 EndAngle=1.5708
    g8: GeomPoint [constr] X=-95 Y=245 Z=0
    g9: GeomPoint [constr] X=95 Y=-245 Z=0
  constraints (22):
    c: Tangent(g0,g4) = -1.5708
    c: Tangent(g0,g5) = -1.5708
    c: Tangent(g1,g5) = -1.5708
    c: Tangent(g1,g6) = -1.5708
    c: Tangent(g2,g6) = -1.5708
    c: Tangent(g2,g7) = -1.5708
    c: Tangent(g3,g7) = -1.5708
    c: Tangent(g3,g4) = -1.5708
    c: Vertical(g0)
    c: Vertical(g2)
    c: Horizontal(g1)
    c: Equal(g5,g6)
    c: Equal(g6,g7)
    c: PointOnObject(g8,g0)
    c: PointOnObject(g8,g3)
    c: PointOnObject(g9,g1)
    c: PointOnObject(g9,g2)
    c: Radius(g4) = 7.5
    c: Distance(g2,g0) = 190
    c: Distance(g1,g3) = 490
    c: Symmetric(g3,g3,g-2)
    c: Symmetric(g3,g1,g-1)
FEATURE [Sketcher::SketchObject] Sketch015  label="interior baffle path"
  ArcFitTolerance = 1e-06
  AttachmentOffset = pos=(0,0,5) rot=(0,0,1;0rad)
  AttachmentSupport = -> [Sketch]
  ExternalTypes = [0]
  FullyConstrained = true
  MakeInternals = false
  MapMode = 2
  Placement = pos=(0,0,5) rot=(0,0,1;0rad)
  _ExternalGeoVersion = 0
  expr: .AttachmentOffset.Base.z = <<v>>.ext_wall
  expr: Constraints[1] = Sketch.Constraints[8] - 2 mm
  expr: Constraints[2] = Sketch.Constraints[9] - 2 mm
  expr: Constraints[4] = Sketch.Constraints[11]
  sketch-geometry (20):
    g0: GeomPoint [constr] X=-85.5 Y=-66.5 Z=0
    g1: GeomPoint [constr] X=-85.5 Y=66.5 Z=0
    g2: GeomPoint [constr] X=20 Y=0 Z=0
    g3: LineSegment [constr] StartX=-85.5 StartY=66.5 StartZ=0 EndX=10.4634 EndY=28.9697 EndZ=0
    g4: LineSegment [constr] StartX=20 StartY=-15 StartZ=0 EndX=20 EndY=15 EndZ=0
    g5: LineSegment [constr] StartX=-85.5 StartY=-66.5 StartZ=0 EndX=10.4634 EndY=-28.9697 EndZ=0
    g6: ArcOfCircle [constr] CenterX=5 CenterY=15 CenterZ=0 NormalX=0 NormalY=0 NormalZ=1 AngleXU=0 Radius=15 StartAngle=0 EndAngle=1.19799
    g7: ArcOfCircle [constr] CenterX=5 CenterY=-15 CenterZ=0 NormalX=0 NormalY=0 NormalZ=1 AngleXU=0 Radius=15 StartAngle=5.08519 EndAngle=6.28319
    g8: LineSegment StartX=17.5 StartY=15 StartZ=0 EndX=17.5 EndY=-15 EndZ=0
    g9: LineSegment StartX=22.5 StartY=-15 StartZ=0 EndX=22.5 EndY=15 EndZ=0
    g10: LineSegment StartX=11.374 StartY=31.2979 StartZ=0 EndX=-84.5894 EndY=68.8283 EndZ=0
    g11: LineSegment StartX=-84.5894 StartY=68.8283 StartZ=0 EndX=-86.4106 EndY=64.1717 EndZ=0
    g12: LineSegment StartX=-86.4106 StartY=64.1717 StartZ=0 EndX=9.55283 EndY=26.6414 EndZ=0
    g13: LineSegment StartX=-86.4106 StartY=-64.1717 StartZ=0 EndX=9.55283 EndY=-26.6414 EndZ=0
    g14: LineSegment StartX=11.374 StartY=-31.2979 StartZ=0 EndX=-84.5894 EndY=-68.8283 EndZ=0
    g15: LineSegment StartX=-84.5894 StartY=-68.8283 StartZ=0 EndX=-86.4106 EndY=-64.1717 EndZ=0
    g16: ArcOfCircle CenterX=5 CenterY=-15 CenterZ=0 NormalX=0 NormalY=0 NormalZ=1 AngleXU=0 Radius=12.5 StartAngle=5.08519 EndAngle=6.28319
    g17: ArcOfCircle CenterX=5 CenterY=-15 CenterZ=0 NormalX=0 NormalY=0 NormalZ=1 AngleXU=0 Radius=17.5 StartAngle=5.08519 EndAngle=6.28319
    g18: ArcOfCircle CenterX=5 CenterY=15 CenterZ=0 NormalX=0 NormalY=0 NormalZ=1 AngleXU=0 Radius=12.5 StartAngle=-9e-16 EndAngle=1.19799
    g19: ArcOfCircle CenterX=5 CenterY=15 CenterZ=0 NormalX=0 NormalY=0 NormalZ=1 AngleXU=0 Radius=17.5 StartAngle=0 EndAngle=1.19799
  constraints (45):
    c: PointOnObject(g2,g-1)
    c: DistanceX(g1,g-1) = 85.5
    c: DistanceY(g0,g1) = 133
    c: Symmetric(g1,g0,g-1)
    c: DistanceX(g-1,g2) = 20
    c: Coincident(g5,g0)
    c: Symmetric(g4,g4,g-1)
    c: DistanceY(g4,g4) = 30
    c: Tangent(g7,g5) = -1.5708
    c: Tangent(g6,g3) = 1.5708
    c: Tangent(g6,g4) = -1.5708
    c: Tangent(g7,g4) = -1.5708
    c: Radius(g6) = 15
    c: Radius(g7) = 15
    c: PointOnObject(g2,g4)
    c: Coincident(g3,g1)
    c: Vertical(g9)
    c: Coincident(g15,g14)
    c: Coincident(g15,g13)
    c: Parallel(g12,g10)
    c: Parallel(g13,g14)
    c: Parallel(g10,g3)
    c: Parallel(g13,g5)
    c: Coincident(g10,g11)
    c: Coincident(g12,g11)
    c: Distance(g11,g11) = 5
    c: Symmetric(g10,g11,g3)
    c: Symmetric(g9,g8,g4)
    c: DistanceX(g8,g9) = 5
    c: DistanceY(g9,g9) = 30
    c: Symmetric(g8,g8,g-1)
    c: Distance(g15,g15) = 5
    c: Symmetric(g13,g14,g5)
    c: Equal(g5,g13)
    c: Equal(g5,g14)
    c: Equal(g3,g10)
    c: Equal(g3,g12)
    c: Coincident(g18,g8)
    c: Tangent(g16,g8) = 1.5708
    c: Tangent(g16,g13) = -1.5708
    c: Tangent(g17,g9) = -1.5708
    c: Tangent(g17,g14) = 1.5708
    c: Tangent(g18,g12) = 1.5708
    c: Tangent(g19,g10) = -1.5708
    c: Tangent(g19,g9) = -1.5708
FEATURE [TechDraw::DrawSVGTemplate] Template001
  EditableTexts = Designed_by_Name=Designed by Name,Drawing_number=Drawing number,FC-Date=24 Mar 2026,FC-SC=1 : 1,FC-SH=2 / 2,FC-Title=wallspeakers prototype v6.1,+3 more (map truncated)
  Height = 210
  Orientation = 1
  Template = /Applications/FreeCAD.app/Contents/Resources/share/Mod/TechDraw/Templates/ISO/A4_Landscape_TD.svg
  Width = 297
FEATURE [TechDraw::DrawSVGTemplate] Template
  EditableTexts = Designed_by_Name=Matt Clark,FC-Date=24 Mar 2026,FC-SC=1 : 2,FC-SH=2 / 2,FC-Title=wallspeakers prototype v6.1,Subtitle=Back view,+1 more (map truncated)
  Height = 210
  Orientation = 1
  Template = /Applications/FreeCAD.app/Contents/Resources/share/Mod/TechDraw/Templates/ISO/A4_Landscape_TD.svg
  Width = 297
FEATURE [TechDraw::DrawSVGTemplate] Template002
  EditableTexts = Designed_by_Name=Matt Clark,FC-Date=24 Mar 2026,FC-SC=1 : 2,FC-SH=3 / 3,FC-Title=wallspeakers prototype v6.1,Subtitle=Enclosure front view,+1 more (map truncated)
  Height = 210
  Orientation = 1
  Template = /Applications/FreeCAD.app/Contents/Resources/share/Mod/TechDraw/Templates/ISO/A4_Landscape_TD.svg
  Width = 297
FEATURE [TechDraw::DrawSVGTemplate] Template003
  EditableTexts = Designed_by_Name=Matt Clark,FC-Date=24 Mar 2026,FC-SH=4 / 4,FC-Title=wallspeakers prototype v6.1,Subtitle=Renderings,+1 more (map truncated)
  Height = 210
  Orientation = 1
  Template = /Applications/FreeCAD.app/Contents/Resources/share/Mod/TechDraw/Templates/ISO/A4_Landscape_TD.svg
  Width = 297
FEATURE [TechDraw::DrawViewImage] ActiveView
  Height = 102.4
  ImageFile = <userpath>/Library/Caches/FreeCAD/Cache/FreeCAD_Doc_eb121f07-895d-47cb-800c-a6bea0ebb6c4_0e058e_119829/Page003ActiveViewwNrP5w.png
  LockPosition = false
  Rotation = 0
  ScaleType = 2
  Width = 128
  X = 82.0287
  Y = 143.216
FEATURE [TechDraw::DrawViewImage] ActiveView001
  Height = 102.4
  ImageFile = <userpath>/Library/Caches/FreeCAD/Cache/FreeCAD_Doc_eb121f07-895d-47cb-800c-a6bea0ebb6c4_0e058e_119829/Page003ActiveView001LiKrpY.png
  LockPosition = false
  Rotation = 0
  ScaleType = 2
  Width = 128
  X = 207.459
  Y = 143.216
FEATURE [TechDraw::DrawPage] Page003  label="renders"
  KeepUpdated = true
  NextBalloonIndex = 1
  ProjectionType = 0
  Template = -> Template003
  Views = -> [ActiveView,ActiveView001]
FEATURE [Part::Feature] Body_cs  label="bmr_cs"
  shape: bbox 195 x 0.0005348 x 48 mm, 0 faces, 0 solids (baked)
FEATURE [Part::Feature] Body_cs001  label="woofer_cs"
  shape: bbox 195 x 0.0005348 x 48 mm, 0 faces, 0 solids (baked)
FEATURE [TechDraw::DrawProjGroupItem] View
  CoarseView = false
  Direction = (0,-1,0)
  Focus = 100
  HardHidden = false
  IsoCount = 0
  IsoHidden = false
  IsoVisible = false
  LockPosition = false
  Perspective = false
  Rotation = 0
  RotationVector = (1,0,0)
  ScaleType = 0
  ScrubCount = 1
  SeamHidden = false
  SeamVisible = false
  SmoothHidden = false
  SmoothVisible = true
  Source = -> [Body_cs]
  Type = 0
  X = 139.152
  XDirection = (1,0,0)
  Y = 92.5034
FEATURE [TechDraw::DrawProjGroupItem] View001
  CoarseView = false
  Direction = (0,-1,0)
  Focus = 100
  HardHidden = false
  IsoCount = 0
  IsoHidden = false
  IsoVisible = false
  LockPosition = false
  Perspective = false
  Rotation = 0
  RotationVector = (1,0,0)
  ScaleType = 0
  ScrubCount = 1
  SeamHidden = false
  SeamVisible = false
  SmoothHidden = false
  SmoothVisible = true
  Source = -> [Body_cs001]
  Type = 0
  X = 139.152
  XDirection = (1,0,0)
  Y = 158.502
FEATURE [TechDraw::DrawViewDimension] Dimension002
  AngleOverride = false
  Arbitrary = false
  ArbitraryTolerances = false
  BoxCorners = (2) [(-97.5,-24,0),(97.5,24,0)]
  EqualTolerance = true
  ExtensionAngle = 0
  FormatSpec = %.2w
  FormatSpecOverTolerance = %+.2w
  FormatSpecUnderTolerance = %+.2w
  Inverted = false
  LineAngle = 0
  LockPosition = false
  MeasureType = 1
  OverTolerance = 0
  References2D = -> [View001]
  Rotation = 0
  ScaleType = 0
  ShowUnits = false
  TheoreticalExact = false
  Type = 1
  UnderTolerance = 0
  UseActualArea = true
  X = -79.25
  Y = -29.5533
FEATURE [TechDraw::DrawViewDimension] Dimension003
  AngleOverride = false
  Arbitrary = false
  ArbitraryTolerances = false
  BoxCorners = (2) [(-97.5,-24,0),(97.5,24,0)]
  EqualTolerance = true
  ExtensionAngle = 0
  FormatSpec = %.2w
  FormatSpecOverTolerance = %+.2w
  FormatSpecUnderTolerance = %+.2w
  Inverted = false
  LineAngle = 0
  LockPosition = false
  MeasureType = 1
  OverTolerance = 0
  References2D = -> [View001]
  Rotation = 0
  ScaleType = 0
  ShowUnits = false
  TheoreticalExact = false
  Type = 2
  UnderTolerance = 0
  UseActualArea = true
  X = -66.4475
  Y = -29.3171
FEATURE [TechDraw::DrawViewDimension] Dimension005
  AngleOverride = false
  Arbitrary = false
  ArbitraryTolerances = false
  BoxCorners = (2) [(-97.5,-24,0),(97.5,24,0)]
  EqualTolerance = true
  ExtensionAngle = 0
  FormatSpec = %.2w
  FormatSpecOverTolerance = %+.2w
  FormatSpecUnderTolerance = %+.2w
  Inverted = false
  LineAngle = 0
  LockPosition = false
  MeasureType = 1
  OverTolerance = 0
  References2D = -> [View001]
  Rotation = 0
  ScaleType = 0
  ShowUnits = false
  TheoreticalExact = false
  Type = 2
  UnderTolerance = 0
  UseActualArea = true
  X = -69.1873
  Y = 13.0686
FEATURE [TechDraw::DrawViewDimension] Dimension010
  AngleOverride = false
  Arbitrary = false
  ArbitraryTolerances = false
  BoxCorners = (2) [(-97.5,-24,0),(97.5,24,0)]
  EqualTolerance = true
  ExtensionAngle = 0
  FormatSpec = %.2w
  FormatSpecOverTolerance = %+.2w
  FormatSpecUnderTolerance = %+.2w
  Inverted = false
  LineAngle = 0
  LockPosition = false
  MeasureType = 1
  OverTolerance = 0
  References2D = -> [View]
  Rotation = 0
  ScaleType = 0
  ShowUnits = false
  TheoreticalExact = false
  Type = 1
  UnderTolerance = 0
  UseActualArea = true
  X = -12.5
  Y = 1.32326
FEATURE [TechDraw::DrawViewDimension] Dimension013
  AngleOverride = false
  Arbitrary = false
  ArbitraryTolerances = false
  BoxCorners = (2) [(-97.5,-24,0),(97.5,24,0)]
  EqualTolerance = true
  ExtensionAngle = 0
  FormatSpec = %.2w
  FormatSpecOverTolerance = %+.2w
  FormatSpecUnderTolerance = %+.2w
  Inverted = false
  LineAngle = 0
  LockPosition = false
  MeasureType = 1
  OverTolerance = 0
  References2D = -> [View]
  Rotation = 0
  ScaleType = 0
  ShowUnits = false
  TheoreticalExact = false
  Type = 0
  UnderTolerance = 0
  UseActualArea = true
  X = 112.527
  Y = -14.9414
FEATURE [TechDraw::DrawViewDimension] Dimension014
  AngleOverride = false
  Arbitrary = false
  ArbitraryTolerances = false
  BoxCorners = (2) [(-97.5,-24,0),(97.5,24,0)]
  EqualTolerance = true
  ExtensionAngle = 0
  FormatSpec = %.2w
  FormatSpecOverTolerance = %+.2w
  FormatSpecUnderTolerance = %+.2w
  Inverted = false
  LineAngle = 0
  LockPosition = false
  MeasureType = 1
  OverTolerance = 0
  References2D = -> [View001]
  Rotation = 0
  ScaleType = 0
  ShowUnits = false
  TheoreticalExact = false
  Type = 2
  UnderTolerance = 0
  UseActualArea = true
  X = 31.0954
  Y = -9.48029
FEATURE [TechDraw::DrawViewDimension] Dimension
  AngleOverride = false
  Arbitrary = false
  ArbitraryTolerances = false
  BoxCorners = (2) [(-97.5,-24,0),(97.5,24,0)]
  EqualTolerance = true
  ExtensionAngle = 0
  FormatSpec = %.2w
  FormatSpecOverTolerance = %+.2w
  FormatSpecUnderTolerance = %+.2w
  Inverted = false
  LineAngle = 0
  LockPosition = false
  MeasureType = 1
  OverTolerance = 0
  References2D = -> [View]
  Rotation = 0
  ScaleType = 0
  ShowUnits = false
  TheoreticalExact = false
  Type = 2
  UnderTolerance = 0
  UseActualArea = true
  X = -88.3712
  Y = 5
FEATURE [TechDraw::DrawViewDimension] Dimension016
  AngleOverride = false
  Arbitrary = false
  ArbitraryTolerances = false
  BoxCorners = (2) [(-97.5,-24,0),(97.5,24,0)]
  EqualTolerance = true
  ExtensionAngle = 0
  FormatSpec = %.2w
  FormatSpecOverTolerance = %+.2w
  FormatSpecUnderTolerance = %+.2w
  Inverted = false
  LineAngle = 0
  LockPosition = false
  MeasureType = 1
  OverTolerance = 0
  References2D = -> [View001]
  Rotation = 0
  ScaleType = 0
  ShowUnits = false
  TheoreticalExact = false
  Type = 0
  UnderTolerance = 0
  UseActualArea = true
  X = 105.443
  Y = -6.825
FEATURE [TechDraw::DrawViewDimension] Dimension018
  AngleOverride = false
  Arbitrary = false
  ArbitraryTolerances = false
  BoxCorners = (2) [(-97.5,-24,0),(97.5,24,0)]
  EqualTolerance = true
  ExtensionAngle = 0
  FormatSpec = %.2w
  FormatSpecOverTolerance = %+.2w
  FormatSpecUnderTolerance = %+.2w
  Inverted = false
  LineAngle = 0
  LockPosition = false
  MeasureType = 1
  OverTolerance = 0
  References2D = -> [View001]
  Rotation = 0
  ScaleType = 0
  ShowUnits = false
  TheoreticalExact = false
  Type = 2
  UnderTolerance = 0
  UseActualArea = true
  X = 71.1934
  Y = 12.7508
FEATURE [TechDraw::DrawViewDimension] Dimension019
  AngleOverride = false
  Arbitrary = false
  ArbitraryTolerances = false
  BoxCorners = (2) [(-97.5,-24,0),(97.5,24,0)]
  EqualTolerance = true
  ExtensionAngle = 0
  FormatSpec = %.2w
  FormatSpecOverTolerance = %+.2w
  FormatSpecUnderTolerance = %+.2w
  Inverted = false
  LineAngle = 0
  LockPosition = false
  MeasureType = 1
  OverTolerance = 0
  References2D = -> [View001]
  Rotation = 0
  ScaleType = 0
  ShowUnits = false
  TheoreticalExact = false
  Type = 2
  UnderTolerance = 0
  UseActualArea = true
  X = 47.9859
  Y = -6.12158
FEATURE [TechDraw::DrawViewDimension] Dimension022
  AngleOverride = false
  Arbitrary = false
  ArbitraryTolerances = false
  BoxCorners = (2) [(-97.5,-24,0),(97.5,24,0)]
  EqualTolerance = true
  ExtensionAngle = 0
  FormatSpec = %.2w
  FormatSpecOverTolerance = %+.2w
  FormatSpecUnderTolerance = %+.2w
  Inverted = false
  LineAngle = 0
  LockPosition = false
  MeasureType = 1
  OverTolerance = 0
  References2D = -> [View]
  Rotation = 0
  ScaleType = 0
  ShowUnits = false
  TheoreticalExact = false
  Type = 1
  UnderTolerance = 0
  UseActualArea = true
  X = -4
  Y = -40.7804
FEATURE [TechDraw::DrawViewDimension] Dimension023
  AngleOverride = false
  Arbitrary = false
  ArbitraryTolerances = false
  BoxCorners = (2) [(-97.5,-24,0),(97.5,24,0)]
  EqualTolerance = true
  ExtensionAngle = 0
  FormatSpec = %.2w
  FormatSpecOverTolerance = %+.2w
  FormatSpecUnderTolerance = %+.2w
  Inverted = false
  LineAngle = 0
  LockPosition = false
  MeasureType = 1
  OverTolerance = 0
  References2D = -> [View]
  Rotation = 0
  ScaleType = 0
  ShowUnits = false
  TheoreticalExact = false
  Type = 2
  UnderTolerance = 0
  UseActualArea = true
  X = -36.0634
  Y = -29.1585
FEATURE [TechDraw::DrawViewDimension] Dimension024
  AngleOverride = false
  Arbitrary = false
  ArbitraryTolerances = false
  BoxCorners = (2) [(-97.5,-24,0),(97.5,24,0)]
  EqualTolerance = true
  ExtensionAngle = 0
  FormatSpec = %.2w
  FormatSpecOverTolerance = %+.2w
  FormatSpecUnderTolerance = %+.2w
  Inverted = false
  LineAngle = 0
  LockPosition = false
  MeasureType = 1
  OverTolerance = 0
  References2D = -> [View]
  Rotation = 0
  ScaleType = 0
  ShowUnits = false
  TheoreticalExact = false
  Type = 1
  UnderTolerance = 0
  UseActualArea = true
  X = 95
  Y = 35.0106
FEATURE [TechDraw::DrawViewDimension] Dimension036
  AngleOverride = false
  Arbitrary = false
  ArbitraryTolerances = false
  BoxCorners = (2) [(-97.5,-24,0),(97.5,24,0)]
  EqualTolerance = true
  ExtensionAngle = 0
  FormatSpec = %.2w
  FormatSpecOverTolerance = %+.2w
  FormatSpecUnderTolerance = %+.2w
  Inverted = false
  LineAngle = 0
  LockPosition = false
  MeasureType = 1
  OverTolerance = 0
  References2D = -> [View]
  Rotation = 0
  ScaleType = 0
  ShowUnits = false
  TheoreticalExact = false
  Type = 2
  UnderTolerance = 0
  UseActualArea = true
  X = -24.5896
  Y = -19.3182
FEATURE [TechDraw::DrawViewDimension] Dimension017
  AngleOverride = false
  Arbitrary = false
  ArbitraryTolerances = false
  BoxCorners = (2) [(-97.5,-24,0),(97.5,24,0)]
  EqualTolerance = true
  ExtensionAngle = 0
  FormatSpec = %.2w
  FormatSpecOverTolerance = %+.2w
  FormatSpecUnderTolerance = %+.2w
  Inverted = false
  LineAngle = 0
  LockPosition = false
  MeasureType = 1
  OverTolerance = 0
  References2D = -> [View001]
  Rotation = 0
  ScaleType = 0
  ShowUnits = false
  TheoreticalExact = false
  Type = 2
  UnderTolerance = 0
  UseActualArea = true
  X = 117.054
  Y = 0
FEATURE [TechDraw::DrawViewDimension] Dimension039
  AngleOverride = false
  Arbitrary = false
  ArbitraryTolerances = false
  BoxCorners = (2) [(-97.5,-24,0),(97.5,24,0)]
  EqualTolerance = true
  ExtensionAngle = 0
  FormatSpec = %.2w
  FormatSpecOverTolerance = %+.2w
  FormatSpecUnderTolerance = %+.2w
  Inverted = false
  LineAngle = 0
  LockPosition = false
  MeasureType = 1
  OverTolerance = 0
  References2D = -> [View001]
  Rotation = 0
  ScaleType = 0
  ShowUnits = false
  TheoreticalExact = false
  Type = 1
  UnderTolerance = 0
  UseActualArea = true
  X = -92.4743
  Y = 32.9307
FEATURE [TechDraw::DrawViewDimension] Dimension040
  AngleOverride = false
  Arbitrary = false
  ArbitraryTolerances = false
  BoxCorners = (2) [(-97.5,-24,0),(97.5,24,0)]
  EqualTolerance = true
  ExtensionAngle = 0
  FormatSpec = %.2w
  FormatSpecOverTolerance = %+.2w
  FormatSpecUnderTolerance = %+.2w
  Inverted = false
  LineAngle = 0
  LockPosition = false
  MeasureType = 1
  OverTolerance = 0
  References2D = -> [View001]
  Rotation = 0
  ScaleType = 0
  ShowUnits = false
  TheoreticalExact = false
  Type = 0
  UnderTolerance = 0
  UseActualArea = true
  X = -83.0706
  Y = 8.26113
FEATURE [App::Point] Origin003
  Role = Origin
FEATURE [Sketcher::SketchObject] Sketch016
  ArcFitTolerance = 1e-06
  AttachmentOffset = pos=(0,0,50) rot=(0,0,1;0rad)
  AttachmentSupport = -> [Origin002]
  ExternalTypes = [0]
  FullyConstrained = true
  MakeInternals = false
  MapMode = 5
  Placement = pos=(0,0,50) rot=(0,0,1;0rad)
  _ExternalGeoVersion = 0
  expr: .AttachmentOffset.Base.z = <<v>>.ext_depth
  expr: Constraints[17] = <<v>>.backplate_width
  expr: Constraints[18] = <<v>>.backplate_height
  expr: Constraints[19] = <<v>>.ext_roundover - <<v>>.rim_width
  sketch-geometry (10):
    g0: LineSegment StartX=-94.9 StartY=237.4 StartZ=0 EndX=-94.9 EndY=-237.4 EndZ=0
    g1: LineSegment StartX=-87.4 StartY=-244.9 StartZ=0 EndX=87.4 EndY=-244.9 EndZ=0
    g2: LineSegment StartX=94.9 StartY=-237.4 StartZ=0 EndX=94.9 EndY=237.4 EndZ=0
    g3: LineSegment StartX=87.4 StartY=244.9 StartZ=0 EndX=-87.4 EndY=244.9 EndZ=0
    g4: ArcOfCircle CenterX=-87.4 CenterY=237.4 CenterZ=0 NormalX=0 NormalY=0 NormalZ=1 AngleXU=0 Radius=7.5 StartAngle=1.5708 EndAngle=3.14159
    g5: ArcOfCircle CenterX=-87.4 CenterY=-237.4 CenterZ=0 NormalX=0 NormalY=0 NormalZ=1 AngleXU=0 Radius=7.5 StartAngle=3.14159 EndAngle=4.71239
    g6: ArcOfCircle CenterX=87.4 CenterY=-237.4 CenterZ=0 NormalX=0 NormalY=0 NormalZ=1 AngleXU=0 Radius=7.5 StartAngle=4.71239 EndAngle=6.28319
    g7: ArcOfCircle CenterX=87.4 CenterY=237.4 CenterZ=0 NormalX=0 NormalY=0 NormalZ=1 AngleXU=0 Radius=7.5 StartAngle=9e-16 EndAngle=1.5708
    g8: GeomPoint [constr] X=-94.9 Y=244.9 Z=0
    g9: GeomPoint [constr] X=94.9 Y=-244.9 Z=0
  constraints (22):
    c: Tangent(g0,g4) = -1.5708
    c: Tangent(g0,g5) = -1.5708
    c: Tangent(g1,g5) = -1.5708
    c: Tangent(g1,g6) = -1.5708
    c: Tangent(g2,g6) = -1.5708
    c: Tangent(g2,g7) = -1.5708
    c: Tangent(g3,g7) = -1.5708
    c: Tangent(g3,g4) = -1.5708
    c: Vertical(g0)
    c: Vertical(g2)
    c: Horizontal(g1)
    c: Equal(g5,g6)
    c: Equal(g6,g7)
    c: PointOnObject(g8,g0)
    c: PointOnObject(g8,g3)
    c: PointOnObject(g9,g1)
    c: PointOnObject(g9,g2)
    c: Distance(g2,g0) = 189.8
    c: Distance(g1,g3) = 489.8
    c: Radius(g6) = 7.5
    c: Symmetric(g3,g3,g-2)
    c: Symmetric(g3,g1,g-1)
FEATURE [PartDesign::Pad] Pad005
  Direction = (0,0,1)
  Length = 5
  Length2 = 10
  Profile = -> Sketch016
  ReferenceAxis = -> Sketch016 [N_Axis]
  Reversed = true
  SideType = 0
  Suppressed = false
  Type = 0
  Type2 = 0
  expr: Length = <<v>>.backplate_thickness
FEATURE [Sketcher::SketchObject] Sketch017
  ArcFitTolerance = 1e-06
  AttachmentSupport = -> [Pad005]
  ExternalTypes = [0]
  FullyConstrained = true
  MakeInternals = false
  MapMode = 5
  Placement = pos=(0,0,50) rot=(0,0,1;0rad)
  _ExternalGeoVersion = 0
  expr: Constraints[11] = Sketch013.Constraints[11]
  expr: Constraints[1] = Sketch013.Constraints[1]
  expr: Constraints[2] = Sketch013.Constraints[2]
  expr: Constraints[8] = Sketch013.Constraints[8]
  expr: Constraints[9] = Sketch013.Constraints[9]
  sketch-geometry (9):
    g0: GeomPoint X=-87.5 Y=237.5 Z=0
    g1: GeomPoint X=87.5 Y=237.5 Z=0
    g2: GeomPoint X=87.5 Y=-237.5 Z=0
    g3: GeomPoint X=-87.5 Y=-237.5 Z=0
    g4: GeomPoint X=-87.5 Y=-67.5 Z=0
    g5: GeomPoint X=-87.5 Y=67.5 Z=0
    g6: GeomPoint X=87.5 Y=67.5 Z=0
    g7: GeomPoint X=87.5 Y=-67.5 Z=0
    g8: GeomPoint X=20 Y=0 Z=0
  constraints (12):
    c: PointOnObject(g8,g-1)
    c: DistanceY(g-1,g0) = 237.5
    c: DistanceX(g0,g-1) = 87.5
    c: Symmetric(g0,g1,g-2)
    c: Symmetric(g5,g6,g-2)
    c: Symmetric(g4,g7,g-2)
    c: Symmetric(g3,g2,g-2)
    c: Symmetric(g2,g1,g-1)
    c: DistanceX(g5,g-1) = 87.5
    c: DistanceY(g4,g5) = 135
    c: Symmetric(g5,g4,g-1)
    c: DistanceX(g-1,g8) = 20
FEATURE [PartDesign::Hole] Hole003
  BaseFeature = -> Pad005
  BaseProfileType = 7
  CustomThreadClearance = 0
  Depth = 5
  DepthType = 0
  Diameter = 4.5
  DrillForDepth = false
  DrillPoint = 1
  DrillPointAngle = 118
  HoleCutCountersinkAngle = 90
  HoleCutCustomValues = false
  HoleCutDepth = 4.5
  HoleCutDiameter = 9
  HoleCutType = 2
  ModelThread = false
  Profile = -> Sketch017
  Suppressed = false
  Tapered = false
  TaperedAngle = 90
  ThreadClass = 0
  ThreadDepth = 5
  ThreadDepthType = 0
  ThreadDiameter = 4
  ThreadDirection = 0
  ThreadFit = 0
  ThreadSize = 11
  ThreadType = 1
  Threaded = false
  UseCustomThreadClearance = false
  expr: Depth = <<v>>.backplate_thickness
FEATURE [TechDraw::DrawViewAnnotation] Annotation
  Font = osifont
  LineSpace = 100
  LockPosition = false
  MaxWidth = -1
  Rotation = 0
  ScaleType = 0
  Text = M4 threaded
  TextSize = 3
  TextStyle = 0
  X = 72.2188
  Y = 114.907
FEATURE [TechDraw::DrawViewAnnotation] Annotation001
  Font = osifont
  LineSpace = 100
  LockPosition = false
  MaxWidth = -1
  Rotation = 0
  ScaleType = 0
  Text = M4 threaded
  TextSize = 3
  TextStyle = 0
  X = 72.0467
  Y = 114.391
FEATURE [TechDraw::DrawViewAnnotation] Annotation002
  Font = osifont
  LineSpace = 100
  LockPosition = false
  MaxWidth = -1
  Rotation = 0
  ScaleType = 0
  Text = M4 threaded
  TextSize = 3
  TextStyle = 0
  X = 72.0467
  Y = 114.391
FEATURE [TechDraw::DrawViewAnnotation] Annotation003
  Font = osifont
  LineSpace = 100
  LockPosition = false
  MaxWidth = -1
  Rotation = 0
  ScaleType = 0
  Text = M4 threaded
  TextSize = 3
  TextStyle = 0
  X = 72.0467
  Y = 114.391
FEATURE [TechDraw::DrawViewAnnotation] Annotation004
  Font = osifont
  LineSpace = 100
  LockPosition = false
  MaxWidth = -1
  Rotation = 0
  ScaleType = 0
  Text = M4 threaded
  TextSize = 3
  TextStyle = 0
  X = 72.2188
  Y = 114.907
FEATURE [TechDraw::DrawViewAnnotation] Annotation005
  Font = osifont
  LineSpace = 100
  LockPosition = false
  MaxWidth = -1
  Rotation = 0
  ScaleType = 0
  Text = M3 threaded
  TextSize = 2.5
  TextStyle = 0
  X = 160.64
  Y = 112.571
FEATURE [TechDraw::DrawViewDimension] Dimension020
  AngleOverride = false
  Arbitrary = false
  ArbitraryTolerances = false
  BoxCorners = (2) [(-97.5,-24,0),(97.5,24,0)]
  EqualTolerance = true
  ExtensionAngle = 0
  FormatSpec = %.2w
  FormatSpecOverTolerance = %+.2w
  FormatSpecUnderTolerance = %+.2w
  Inverted = false
  LineAngle = 0
  LockPosition = false
  MeasureType = 1
  OverTolerance = 0
  References2D = -> [View]
  Rotation = 0
  ScaleType = 0
  ShowUnits = false
  TheoreticalExact = false
  Type = 0
  UnderTolerance = 0
  UseActualArea = true
  X = -55.9422
  Y = -35.2571
FEATURE [TechDraw::DrawViewDimension] Dimension048
  AngleOverride = false
  Arbitrary = false
  ArbitraryTolerances = false
  BoxCorners = (2) [(-97.5,-24,0),(97.5,24,0)]
  EqualTolerance = true
  ExtensionAngle = 0
  FormatSpec = %.2w
  FormatSpecOverTolerance = %+.2w
  FormatSpecUnderTolerance = %+.2w
  Inverted = false
  LineAngle = 0
  LockPosition = false
  MeasureType = 1
  OverTolerance = 0
  References2D = -> [View]
  Rotation = 0
  ScaleType = 0
  ShowUnits = false
  TheoreticalExact = false
  Type = 2
  UnderTolerance = 0
  UseActualArea = true
  X = -47.4615
  Y = -5.7216
FEATURE [TechDraw::DrawViewDimension] Dimension049
  AngleOverride = false
  Arbitrary = false
  ArbitraryTolerances = false
  BoxCorners = (2) [(-97.5,-24,0),(97.5,24,0)]
  EqualTolerance = true
  ExtensionAngle = 0
  FormatSpec = %.2w
  FormatSpecOverTolerance = %+.2w
  FormatSpecUnderTolerance = %+.2w
  Inverted = false
  LineAngle = 0
  LockPosition = false
  MeasureType = 1
  OverTolerance = 0
  References2D = -> [View]
  Rotation = 0
  ScaleType = 0
  ShowUnits = false
  TheoreticalExact = false
  Type = 2
  UnderTolerance = 0
  UseActualArea = true
  X = -112.276
  Y = -22.3181
FEATURE [TechDraw::DrawPage] Page001  label="driver cross sections"
  KeepUpdated = true
  NextBalloonIndex = 1
  ProjectionType = 0
  Template = -> Template001
  Views = -> [View,View001,Dimension002,Dimension003,Dimension005,Dimension010,Dimension013,Dimension014,Dimension,Dimension016,Dimension017,Dimension018,Dimension019,Dimension020,Dimension022,Dimension023,Dimension024,Dimension036,Dimension039,Dimension040,Dimension048,Dimension049]
FEATURE [PartDesign::Thickness] Thickness
  Base = -> Fillet [Face4]
  BaseFeature = -> Fillet
  Intersection = false
  Join = 0
  Mode = 0
  Reversed = true
  SupportTransform = false
  Suppressed = false
  Value = 5
  expr: Value = <<v>>.ext_wall
FEATURE [PartDesign::Pad] Pad006
  BaseFeature = -> Thickness
  Direction = (0,0,1)
  Length = 45
  Length2 = 10
  Profile = -> Sketch004
  ReferenceAxis = -> Sketch004 [N_Axis]
  Reversed = true
  SideType = 0
  Suppressed = false
  Type = 0
  Type2 = 0
  expr: Length = <<v>>.ext_depth - <<v>>.ext_wall
FEATURE [PartDesign::Pocket] Pocket004  label="rim pocket"
  BaseFeature = -> Pad006
  Direction = (0,0,-1)
  Length = 5.9
  Length2 = 5
  Profile = -> Sketch014
  ReferenceAxis = -> Sketch014 [N_Axis]
  SideType = 0
  Suppressed = false
  Type = 0
  Type2 = 0
  expr: Length = <<v>>.backplate_rebate
FEATURE [PartDesign::Pad] Pad004  label="interior baffle"
  BaseFeature = -> Pocket004
  Direction = (0,0,1)
  Length = 39.1
  Length2 = 10
  Profile = -> Sketch015
  ReferenceAxis = -> Sketch015 [N_Axis]
  SideType = 0
  Suppressed = false
  Type = 0
  Type2 = 0
  expr: Length = <<v>>.int_depth
FEATURE [PartDesign::Pad] Pad002  label="woofer support ring"
  BaseFeature = -> Pad004
  Direction = (0,0,1)
  Length = 6
  Length2 = 10
  Profile = -> Sketch006
  ReferenceAxis = -> Sketch006 [N_Axis]
  SideType = 0
  Suppressed = false
  Type = 0
  Type2 = 0
  expr: Length = VarSet001.woofer_support_thickness
FEATURE [PartDesign::Pocket] Pocket  label="woofer rebate pocket"
  BaseFeature = -> Pad002
  Direction = (0,0,-1)
  Length = 7.2
  Length2 = 5
  Profile = -> Sketch005
  ReferenceAxis = -> Sketch005 [N_Axis]
  Reversed = true
  SideType = 0
  Suppressed = false
  Type = 0
  Type2 = 0
  expr: Length = VarSet001.woofer_rebate_depth
FEATURE [PartDesign::Chamfer] Chamfer001  label="woofer rebate chamfer"
  Angle = 45
  Base = -> Pocket [Edge43,Edge42]
  BaseFeature = -> Pocket
  ChamferType = 1
  FlipDirection = false
  Size = 8
  Size2 = 1
  SupportTransform = false
  Suppressed = false
  UseAllEdges = false
  expr: Size = <<v>>.woofer_chamfer_width
  expr: Size2 = <<v>>.woofer_chamfer_depth
FEATURE [PartDesign::Pocket] Pocket001  label="woofer holes"
  BaseFeature = -> Chamfer001
  Direction = (0,0,-1)
  Length = 20
  Length2 = 5
  Profile = -> Sketch007
  ReferenceAxis = -> Sketch007 [N_Axis]
  Reversed = true
  SideType = 0
  Suppressed = false
  Type = 0
  Type2 = 0
FEATURE [Sketcher::SketchObject] Sketch018
  ArcFitTolerance = 1e-06
  AttachmentSupport = -> [Pad005]
  ExternalTypes = [0]
  FullyConstrained = true
  MakeInternals = false
  MapMode = 5
  Placement = pos=(0,0,50) rot=(0,0,1;0rad)
  _ExternalGeoVersion = 0
  expr: Constraints[19] = <<v>>.ext_height + 5 mm
  expr: Constraints[20] = <<v>>.ext_width / 2 + 5 mm
  sketch-geometry (8):
    g0: LineSegment StartX=-102.5 StartY=6 StartZ=0 EndX=-102.5 EndY=-6 EndZ=0
    g1: LineSegment StartX=-102.5 StartY=-6 StartZ=0 EndX=-6 EndY=-6 EndZ=0
    g2: LineSegment StartX=-6 StartY=-6 StartZ=0 EndX=-6 EndY=-250 EndZ=0
    g3: LineSegment StartX=-6 StartY=-250 StartZ=0 EndX=6 EndY=-250 EndZ=0
    g4: LineSegment StartX=6 StartY=-250 StartZ=0 EndX=6 EndY=250 EndZ=0
    g5: LineSegment StartX=6 StartY=250 StartZ=0 EndX=-6 EndY=250 EndZ=0
    g6: LineSegment StartX=-6 StartY=250 StartZ=0 EndX=-6 EndY=6 EndZ=0
    g7: LineSegment StartX=-6 StartY=6 StartZ=0 EndX=-102.5 EndY=6 EndZ=0
  constraints (21):
    c: Vertical(g0)
    c: Coincident(g0,g1)
    c: Horizontal(g1)
    c: Coincident(g1,g2)
    c: Vertical(g2)
    c: Coincident(g2,g3)
    c: Coincident(g3,g4)
    c: Coincident(g4,g5)
    c: Coincident(g5,g6)
    c: Vertical(g6)
    c: Coincident(g6,g7)
    c: Coincident(g7,g0)
    c: Horizontal(g7)
    c: Horizontal(g3)
    c: Symmetric(g4,g3,g-1)
    c: Symmetric(g5,g4,g-2)
    c: Symmetric(g6,g1,g-1)
    c: DistanceY(g0,g0) = 12
    c: DistanceX(g5,g5) = 12
    c: DistanceY(g4,g4) = 500
    c: DistanceX(g0,g-1) = 102.5
FEATURE [PartDesign::Pocket] Pocket005
  BaseFeature = -> Hole003
  Direction = (0,0,-1)
  Length = 2
  Length2 = 5
  Profile = -> Sketch018
  ReferenceAxis = -> Sketch018 [N_Axis]
  SideType = 0
  Suppressed = false
  Type = 0
  Type2 = 0
FEATURE [Sketcher::SketchObject] Sketch019
  ArcFitTolerance = 1e-06
  AttachmentSupport = -> [Pad005]
  ExternalTypes = [0]
  FullyConstrained = true
  MakeInternals = false
  MapMode = 5
  Placement = pos=(0,0,50) rot=(0,0,1;0rad)
  _ExternalGeoVersion = 0
  sketch-geometry (12):
    g0: LineSegment StartX=-8 StartY=7 StartZ=0 EndX=-8 EndY=-7 EndZ=0
    g1: LineSegment StartX=-7 StartY=-8 StartZ=0 EndX=7 EndY=-8 EndZ=0
    g2: LineSegment StartX=8 StartY=-7 StartZ=0 EndX=8 EndY=7 EndZ=0
    g3: LineSegment StartX=7 StartY=8 StartZ=0 EndX=-7 EndY=8 EndZ=0
    g4: ArcOfCircle CenterX=7 CenterY=7 CenterZ=0 NormalX=0 NormalY=0 NormalZ=1 AngleXU=0 Radius=1 StartAngle=0 EndAngle=1.5708
    g5: GeomPoint [constr] X=8 Y=8 Z=0
    g6: ArcOfCircle CenterX=7 CenterY=-7 CenterZ=0 NormalX=0 NormalY=0 NormalZ=1 AngleXU=0 Radius=1 StartAngle=4.71239 EndAngle=6.28319
    g7: GeomPoint [constr] X=8 Y=-8 Z=0
    g8: ArcOfCircle CenterX=-7 CenterY=-7 CenterZ=0 NormalX=0 NormalY=0 NormalZ=1 AngleXU=0 Radius=1 StartAngle=3.14159 EndAngle=4.71239
    g9: GeomPoint [constr] X=-8 Y=-8 Z=0
    g10: ArcOfCircle CenterX=-7 CenterY=7 CenterZ=0 NormalX=0 NormalY=0 NormalZ=1 AngleXU=0 Radius=1 StartAngle=1.5708 EndAngle=3.14159
    g11: GeomPoint [constr] X=-8 Y=8 Z=0
  constraints (26):
    c: Vertical(g0)
    c: Horizontal(g1)
    c: Symmetric(g5,g11,g-2)
    c: Symmetric(g5,g7,g-1)
    c: DistanceY(g7,g5) = 16
    c: DistanceX(g11,g5) = 16
    c: PointOnObject(g5,g3)
    c: PointOnObject(g5,g2)
    c: Tangent(g3,g4) = -1.5708
    c: Tangent(g2,g4) = -1.5708
    c: PointOnObject(g7,g1)
    c: PointOnObject(g7,g2)
    c: Tangent(g1,g6) = -1.5708
    c: Tangent(g2,g6) = -1.5708
    c: PointOnObject(g9,g0)
    c: PointOnObject(g9,g1)
    c: Tangent(g0,g8) = -1.5708
    c: Tangent(g1,g8) = -1.5708
    c: PointOnObject(g11,g3)
    c: PointOnObject(g11,g0)
    c: Tangent(g3,g10) = -1.5708
    c: Tangent(g0,g10) = -1.5708
    c: Radius(g4) = 1
    c: Equal(g4,g6)
    c: Equal(g4,g8)
    c: Equal(g4,g10)
FEATURE [PartDesign::Pocket] Pocket006
  BaseFeature = -> Pocket005
  Direction = (0,0,-1)
  Length = 5
  Length2 = 5
  Profile = -> Sketch019
  ReferenceAxis = -> Sketch019 [N_Axis]
  SideType = 0
  Suppressed = false
  Type = 0
  Type2 = 0
FEATURE [PartDesign::Body] Body001  label="backplate"
  AllowCompound = false
  Group = -> [Sketch016,Pad005,Sketch019,Sketch017,Hole003,Sketch018,Pocket005,Pocket006]
  Origin = -> Origin002
  Tip = -> Pocket006
FEATURE [PartDesign::Chamfer] Chamfer003  label="woofer backside chamfer"
  Angle = 45
  Base = -> Pocket001 [Edge88,Edge70,Edge89,Edge130]
  BaseFeature = -> Pocket001
  ChamferType = 0
  FlipDirection = false
  Size = 3
  Size2 = 1
  SupportTransform = false
  Suppressed = false
  UseAllEdges = false
FEATURE [PartDesign::Hole] Hole  label="woofer screw holes"
  BaseFeature = -> Chamfer003
  BaseProfileType = 7
  CustomThreadClearance = 0
  Depth = 25
  DepthType = 0
  Diameter = 4.5
  DrillForDepth = false
  DrillPoint = 1
  DrillPointAngle = 118
  HoleCutCountersinkAngle = 90
  HoleCutCustomValues = false
  HoleCutDepth = 0
  HoleCutDiameter = 0
  HoleCutType = 0
  ModelThread = false
  Profile = -> Sketch011
  Reversed = true
  Suppressed = false
  Tapered = false
  TaperedAngle = 90
  ThreadClass = 0
  ThreadDepth = 25
  ThreadDepthType = 0
  ThreadDiameter = 4
  ThreadDirection = 0
  ThreadFit = 0
  ThreadSize = 11
  ThreadType = 1
  Threaded = false
  UseCustomThreadClearance = false
FEATURE [PartDesign::Pad] Pad003  label="bmr support ring"
  BaseFeature = -> Hole
  Direction = (0,0,1)
  Length = 3
  Length2 = 10
  Profile = -> Sketch009
  ReferenceAxis = -> Sketch009 [N_Axis]
  SideType = 0
  Suppressed = false
  Type = 0
  Type2 = 0
  expr: Length = VarSet001.bmr_support_thickness
FEATURE [PartDesign::Pocket] Pocket002  label="bmr rebate pocket"
  BaseFeature = -> Pad003
  Direction = (0,0,-1)
  Length = 5.4
  Length2 = 5
  Profile = -> Sketch008
  ReferenceAxis = -> Sketch008 [N_Axis]
  Reversed = true
  SideType = 0
  Suppressed = false
  Type = 0
  Type2 = 0
  expr: Length = VarSet001.bmr_rebate_depth
FEATURE [PartDesign::Chamfer] Chamfer  label="bmr rebate chamfer"
  Angle = 45
  Base = -> Pocket002 [Edge44]
  BaseFeature = -> Pocket002
  ChamferType = 1
  FlipDirection = false
  Size = 6
  Size2 = 1.5
  SupportTransform = false
  Suppressed = false
  UseAllEdges = false
  expr: Size = <<v>>.bmr_chamfer_width
  expr: Size2 = <<v>>.bmr_chamfer_depth
FEATURE [PartDesign::Pocket] Pocket003  label="bmr hole"
  BaseFeature = -> Chamfer
  Direction = (0,0,-1)
  Length = 20
  Length2 = 5
  Profile = -> Sketch010
  ReferenceAxis = -> Sketch010 [N_Axis]
  Reversed = true
  SideType = 0
  Suppressed = false
  Type = 0
  Type2 = 0
FEATURE [PartDesign::Chamfer] Chamfer002  label="bmr backside chamfer"
  Angle = 45
  Base = -> Pocket003 [Edge84,Edge137]
  BaseFeature = -> Pocket003
  ChamferType = 0
  FlipDirection = false
  Size = 3
  Size2 = 1
  SupportTransform = false
  Suppressed = false
  UseAllEdges = false
FEATURE [PartDesign::Hole] Hole001  label="bmr screw holes"
  BaseFeature = -> Chamfer002
  BaseProfileType = 7
  CustomThreadClearance = 0
  Depth = 25
  DepthType = 0
  Diameter = 2.5
  DrillForDepth = false
  DrillPoint = 1
  DrillPointAngle = 118
  HoleCutCountersinkAngle = 90
  HoleCutCustomValues = false
  HoleCutDepth = 0
  HoleCutDiameter = 0
  HoleCutType = 0
  ModelThread = false
  Profile = -> Sketch012
  Reversed = true
  Suppressed = false
  Tapered = false
  TaperedAngle = 90
  ThreadClass = 0
  ThreadDepth = 25
  ThreadDepthType = 0
  ThreadDiameter = 3
  ThreadDirection = 0
  ThreadFit = 0
  ThreadSize = 9
  ThreadType = 1
  Threaded = true
  UseCustomThreadClearance = false
FEATURE [PartDesign::Hole] Hole002  label="post screw holes"
  BaseFeature = -> Hole001
  BaseProfileType = 7
  CustomThreadClearance = 0
  Depth = 25
  DepthType = 0
  Diameter = 3.3
  DrillForDepth = false
  DrillPoint = 1
  DrillPointAngle = 118
  HoleCutCountersinkAngle = 90
  HoleCutCustomValues = false
  HoleCutDepth = 0
  HoleCutDiameter = 0
  HoleCutType = 0
  ModelThread = false
  Profile = -> Sketch013
  Suppressed = false
  Tapered = false
  TaperedAngle = 90
  ThreadClass = 0
  ThreadDepth = 25
  ThreadDepthType = 0
  ThreadDiameter = 4
  ThreadDirection = 0
  ThreadFit = 0
  ThreadSize = 11
  ThreadType = 1
  Threaded = true
  UseCustomThreadClearance = false
FEATURE [PartDesign::Fillet] Fillet001
  Base = -> Hole002 [Edge216,Edge74,Edge278,Edge86,Edge221,Edge307,Edge88,Edge82]
  BaseFeature = -> Hole002
  Radius = 5
  SupportTransform = false
  Suppressed = false
  UseAllEdges = false
FEATURE [PartDesign::Body] Body
  AllowCompound = false
  Group = -> [Sketch002,Sketch,Sketch003,Pad,Fillet,Thickness,Pad006,Sketch004,Pocket004,Pad004,Pad002,Pocket,Chamfer001,Pocket001,Chamfer003,Hole,Pad003,Pocket002,Chamfer,Pocket003,Chamfer002,Hole001,Sketch005,Sketch006,Sketch007,Sketch008,Sketch009,Sketch010,Sketch011,Sketch012,Sketch013,Hole002,Sketch014,Sketch015,Fillet001]
  Origin = -> Origin
  Tip = -> Fillet001
FEATURE [TechDraw::DrawProjGroupItem] View002
  CoarseView = false
  Direction = (0,0,1)
  Focus = 100
  HardHidden = false
  IsoCount = 0
  IsoHidden = false
  IsoVisible = false
  LockPosition = false
  Perspective = false
  Rotation = 0
  RotationVector = (1,0,0)
  Scale = 0.5
  ScaleType = 2
  ScrubCount = 1
  SeamHidden = false
  SeamVisible = false
  SmoothHidden = false
  SmoothVisible = true
  Source = -> [Body]
  Type = 0
  X = 146.976
  XDirection = (3e-16,-1,0)
  Y = 133.819
FEATURE [TechDraw::DrawProjGroupItem] View003
  CoarseView = false
  Direction = (0,0,-1)
  Focus = 100
  HardHidden = false
  IsoCount = 0
  IsoHidden = false
  IsoVisible = false
  LockPosition = false
  Perspective = false
  Rotation = 0
  RotationVector = (1,0,0)
  Scale = 0.5
  ScaleType = 2
  ScrubCount = 1
  SeamHidden = false
  SeamVisible = false
  SmoothHidden = false
  SmoothVisible = true
  Source = -> [Body]
  Type = 0
  X = 147.219
  XDirection = (1e-16,1,0)
  Y = 134.934
FEATURE [TechDraw::DrawViewDimension] Dimension026
  AngleOverride = false
  Arbitrary = false
  ArbitraryTolerances = false
  BoxCorners = (2) [(-123.75,-48.75,-1e-07),(123.75,48.75,1e-07)]
  EqualTolerance = true
  ExtensionAngle = 0
  FormatSpec = ⌀%.2w
  FormatSpecOverTolerance = %+.2w
  FormatSpecUnderTolerance = %+.2w
  Inverted = false
  LineAngle = 0
  LockPosition = false
  MeasureType = 1
  OverTolerance = 0
  References2D = -> [View003]
  Rotation = 0
  ScaleType = 0
  ShowUnits = false
  TheoreticalExact = false
  Type = 5
  UnderTolerance = 0
  UseActualArea = true
  X = -67.7964
  Y = 13.2495
FEATURE [TechDraw::DrawViewDimension] Dimension027
  AngleOverride = false
  Arbitrary = false
  ArbitraryTolerances = false
  BoxCorners = (2) [(-123.75,-48.75,-1e-07),(123.75,48.75,1e-07)]
  EqualTolerance = true
  ExtensionAngle = 0
  FormatSpec = ⌀%.2w
  FormatSpecOverTolerance = %+.2w
  FormatSpecUnderTolerance = %+.2w
  Inverted = false
  LineAngle = 0
  LockPosition = false
  MeasureType = 1
  OverTolerance = 0
  References2D = -> [View003]
  Rotation = 0
  ScaleType = 0
  ShowUnits = false
  TheoreticalExact = false
  Type = 5
  UnderTolerance = 0
  UseActualArea = true
  X = -46.8036
  Y = 8.77568
FEATURE [TechDraw::DrawViewDimension] Dimension028
  AngleOverride = false
  Arbitrary = false
  ArbitraryTolerances = false
  BoxCorners = (2) [(-123.75,-48.75,-1e-07),(123.75,48.75,1e-07)]
  EqualTolerance = true
  ExtensionAngle = 0
  FormatSpec = ⌀%.2w
  FormatSpecOverTolerance = %+.2w
  FormatSpecUnderTolerance = %+.2w
  Inverted = false
  LineAngle = 0
  LockPosition = false
  MeasureType = 1
  OverTolerance = 0
  References2D = -> [View003]
  Rotation = 0
  ScaleType = 0
  ShowUnits = false
  TheoreticalExact = false
  Type = 5
  UnderTolerance = 0
  UseActualArea = true
  X = -9.02964
  Y = 8.42399
FEATURE [TechDraw::DrawViewDimension] Dimension029
  AngleOverride = false
  Arbitrary = false
  ArbitraryTolerances = false
  BoxCorners = (2) [(-123.75,-48.75,-1e-07),(123.75,48.75,1e-07)]
  EqualTolerance = true
  ExtensionAngle = 0
  FormatSpec = ⌀%.2w
  FormatSpecOverTolerance = %+.2w
  FormatSpecUnderTolerance = %+.2w
  Inverted = false
  LineAngle = 0
  LockPosition = false
  MeasureType = 1
  OverTolerance = 0
  References2D = -> [View003]
  Rotation = 0
  ScaleType = 0
  ShowUnits = false
  TheoreticalExact = false
  Type = 5
  UnderTolerance = 0
  UseActualArea = true
  X = 8.25946
  Y = 8.43153
FEATURE [TechDraw::DrawViewDimension] Dimension030
  AngleOverride = false
  Arbitrary = false
  ArbitraryTolerances = false
  BoxCorners = (2) [(-123.75,-48.75,-1e-07),(123.75,48.75,1e-07)]
  EqualTolerance = true
  ExtensionAngle = 0
  FormatSpec = %.2w
  FormatSpecOverTolerance = %+.2w
  FormatSpecUnderTolerance = %+.2w
  Inverted = false
  LineAngle = 0
  LockPosition = false
  MeasureType = 1
  OverTolerance = 0
  References2D = -> [View003]
  Rotation = 0
  ScaleType = 0
  ShowUnits = false
  TheoreticalExact = false
  Type = 1
  UnderTolerance = 0
  UseActualArea = true
  X = 61.2867
  Y = -57.9698
FEATURE [TechDraw::DrawViewDimension] Dimension031
  AngleOverride = false
  Arbitrary = false
  ArbitraryTolerances = false
  BoxCorners = (2) [(-123.75,-48.75,-1e-07),(123.75,48.75,1e-07)]
  EqualTolerance = true
  ExtensionAngle = 0
  FormatSpec = %.2w
  FormatSpecOverTolerance = %+.2w
  FormatSpecUnderTolerance = %+.2w
  Inverted = false
  LineAngle = 0
  LockPosition = false
  MeasureType = 1
  OverTolerance = 0
  References2D = -> [View003]
  Rotation = 0
  ScaleType = 0
  ShowUnits = false
  TheoreticalExact = false
  Type = 2
  UnderTolerance = 0
  UseActualArea = true
  X = -24.5474
  Y = -23.3833
FEATURE [TechDraw::DrawViewDimension] Dimension032
  AngleOverride = false
  Arbitrary = false
  ArbitraryTolerances = false
  BoxCorners = (2) [(-123.75,-48.75,-1e-07),(123.75,48.75,1e-07)]
  EqualTolerance = true
  ExtensionAngle = 0
  FormatSpec = %.2w
  FormatSpecOverTolerance = %+.2w
  FormatSpecUnderTolerance = %+.2w
  Inverted = false
  LineAngle = 0
  LockPosition = false
  MeasureType = 1
  OverTolerance = 0
  References2D = -> [View003]
  Rotation = 0
  ScaleType = 0
  ShowUnits = false
  TheoreticalExact = false
  Type = 0
  UnderTolerance = 0
  UseActualArea = true
  X = 119.722
  Y = 62.9969
FEATURE [TechDraw::DrawViewDimension] Dimension033
  AngleOverride = false
  Arbitrary = false
  ArbitraryTolerances = false
  BoxCorners = (2) [(-123.75,-48.75,-1e-07),(123.75,48.75,1e-07)]
  EqualTolerance = true
  ExtensionAngle = 0
  FormatSpec = %.2w
  FormatSpecOverTolerance = %+.2w
  FormatSpecUnderTolerance = %+.2w
  Inverted = false
  LineAngle = 0
  LockPosition = false
  MeasureType = 1
  OverTolerance = 0
  References2D = -> [View003]
  Rotation = 0
  ScaleType = 0
  ShowUnits = false
  TheoreticalExact = false
  Type = 0
  UnderTolerance = 0
  UseActualArea = true
  X = 127.063
  Y = -61.2391
FEATURE [TechDraw::DrawViewDimension] Dimension034
  AngleOverride = false
  Arbitrary = false
  ArbitraryTolerances = false
  BoxCorners = (2) [(-123.75,-48.75,-1e-07),(123.75,48.75,1e-07)]
  EqualTolerance = true
  ExtensionAngle = 0
  FormatSpec = %.2w
  FormatSpecOverTolerance = %+.2w
  FormatSpecUnderTolerance = %+.2w
  Inverted = false
  LineAngle = 0
  LockPosition = false
  MeasureType = 1
  OverTolerance = 0
  References2D = -> [View003]
  Rotation = 0
  ScaleType = 0
  ShowUnits = false
  TheoreticalExact = false
  Type = 0
  UnderTolerance = 0
  UseActualArea = true
  X = 69.1681
  Y = 13.1938
FEATURE [TechDraw::DrawViewDimension] Dimension035
  AngleOverride = false
  Arbitrary = false
  ArbitraryTolerances = false
  BoxCorners = (2) [(-123.75,-48.75,-1e-07),(123.75,48.75,1e-07)]
  EqualTolerance = true
  ExtensionAngle = 0
  FormatSpec = %.2w
  FormatSpecOverTolerance = %+.2w
  FormatSpecUnderTolerance = %+.2w
  Inverted = false
  LineAngle = 0
  LockPosition = false
  MeasureType = 1
  OverTolerance = 0
  References2D = -> [View003]
  Rotation = 0
  ScaleType = 0
  ShowUnits = false
  TheoreticalExact = false
  Type = 0
  UnderTolerance = 0
  UseActualArea = true
  X = -12.2423
  Y = -38.2173
FEATURE [TechDraw::DrawViewDimension] Dimension041
  AngleOverride = false
  Arbitrary = false
  ArbitraryTolerances = false
  BoxCorners = (2) [(-123.75,-48.75,-1e-07),(123.75,48.75,1e-07)]
  EqualTolerance = true
  ExtensionAngle = 0
  FormatSpec = ⌀%.2w
  FormatSpecOverTolerance = %+.2w
  FormatSpecUnderTolerance = %+.2w
  Inverted = false
  LineAngle = 0
  LockPosition = false
  MeasureType = 1
  OverTolerance = 0
  References2D = -> [View002]
  Rotation = 0
  ScaleType = 0
  ShowUnits = false
  TheoreticalExact = false
  Type = 5
  UnderTolerance = 0
  UseActualArea = true
  X = -84.7852
  Y = -0.99516
FEATURE [TechDraw::DrawViewDimension] Dimension042
  AngleOverride = false
  Arbitrary = false
  ArbitraryTolerances = false
  BoxCorners = (2) [(-123.75,-48.75,-1e-07),(123.75,48.75,1e-07)]
  EqualTolerance = true
  ExtensionAngle = 0
  FormatSpec = ⌀%.2w
  FormatSpecOverTolerance = %+.2w
  FormatSpecUnderTolerance = %+.2w
  Inverted = false
  LineAngle = 0
  LockPosition = false
  MeasureType = 1
  OverTolerance = 0
  References2D = -> [View002]
  Rotation = 0
  ScaleType = 0
  ShowUnits = false
  TheoreticalExact = false
  Type = 5
  UnderTolerance = 0
  UseActualArea = true
  X = -77.1872
  Y = 10.7151
FEATURE [TechDraw::DrawViewDimension] Dimension043
  AngleOverride = false
  Arbitrary = false
  ArbitraryTolerances = false
  BoxCorners = (2) [(-123.75,-48.75,0),(123.75,48.75,0)]
  EqualTolerance = true
  ExtensionAngle = 0
  FormatSpec = %.2w
  FormatSpecOverTolerance = %+.2w
  FormatSpecUnderTolerance = %+.2w
  Inverted = false
  LineAngle = 0
  LockPosition = false
  MeasureType = 1
  OverTolerance = 0
  References2D = -> [View002]
  Rotation = 0
  ScaleType = 0
  ShowUnits = false
  TheoreticalExact = false
  Type = 0
  UnderTolerance = 0
  UseActualArea = true
  X = -6.90557
  Y = -26.6256
FEATURE [TechDraw::DrawViewDimension] Dimension044
  AngleOverride = false
  Arbitrary = false
  ArbitraryTolerances = false
  BoxCorners = (2) [(-123.75,-48.75,0),(123.75,48.75,0)]
  EqualTolerance = true
  ExtensionAngle = 0
  FormatSpec = ⌀%.2w
  FormatSpecOverTolerance = %+.2w
  FormatSpecUnderTolerance = %+.2w
  Inverted = false
  LineAngle = 0
  LockPosition = false
  MeasureType = 1
  OverTolerance = 0
  References2D = -> [View002]
  Rotation = 0
  ScaleType = 0
  ShowUnits = false
  TheoreticalExact = false
  Type = 5
  UnderTolerance = 0
  UseActualArea = true
  X = -6.02985
  Y = -15.4398
FEATURE [TechDraw::DrawViewDimension] Dimension045
  AngleOverride = false
  Arbitrary = false
  ArbitraryTolerances = false
  BoxCorners = (2) [(-123.75,-48.75,0),(123.75,48.75,0)]
  EqualTolerance = true
  ExtensionAngle = 0
  FormatSpec = ⌀%.2w
  FormatSpecOverTolerance = %+.2w
  FormatSpecUnderTolerance = %+.2w
  Inverted = false
  LineAngle = 0
  LockPosition = false
  MeasureType = 1
  OverTolerance = 0
  References2D = -> [View002]
  Rotation = 0
  ScaleType = 0
  ShowUnits = false
  TheoreticalExact = false
  Type = 5
  UnderTolerance = 0
  UseActualArea = true
  X = 4.25424
  Y = -21.6438
FEATURE [TechDraw::DrawViewDimension] Dimension046
  AngleOverride = false
  Arbitrary = false
  ArbitraryTolerances = false
  BoxCorners = (2) [(-123.75,-48.75,-1e-07),(123.75,48.75,1e-07)]
  EqualTolerance = true
  ExtensionAngle = 0
  FormatSpec = ⌀%.2w
  FormatSpecOverTolerance = %+.2w
  FormatSpecUnderTolerance = %+.2w
  Inverted = false
  LineAngle = 0
  LockPosition = false
  MeasureType = 1
  OverTolerance = 0
  References2D = -> [View002]
  Rotation = 0
  ScaleType = 0
  ShowUnits = false
  TheoreticalExact = false
  Type = 5
  UnderTolerance = 0
  UseActualArea = true
  X = -57.5067
  Y = -55.5981
FEATURE [TechDraw::DrawViewAnnotation] Annotation006
  Font = osifont
  LineSpace = 100
  LockPosition = false
  MaxWidth = -1
  Owner = -> View002
  Rotation = 0
  ScaleType = 0
  Text = M4 threaded
  TextSize = 4
  TextStyle = 0
  X = -102.151
  Y = -39.0017
FEATURE [TechDraw::DrawProjGroupItem] View004
  CoarseView = false
  Direction = (0,-1,0)
  Focus = 100
  HardHidden = false
  IsoCount = 0
  IsoHidden = false
  IsoVisible = false
  LockPosition = false
  Perspective = false
  Rotation = 0
  RotationVector = (1,0,0)
  Scale = 0.5
  ScaleType = 2
  ScrubCount = 1
  SeamHidden = false
  SeamVisible = false
  SmoothHidden = false
  SmoothVisible = true
  Source = -> [Body]
  Type = 0
  X = 79.4991
  XDirection = (-1,0,1e-16)
  Y = 50.4532
FEATURE [TechDraw::DrawViewDimension] Dimension047
  AngleOverride = false
  Arbitrary = false
  ArbitraryTolerances = false
  BoxCorners = (2) [(-48.75,-12,-1e-07),(48.75,12,1e-07)]
  EqualTolerance = true
  ExtensionAngle = 0
  FormatSpec = R%.2w
  FormatSpecOverTolerance = %+.2w
  FormatSpecUnderTolerance = %+.2w
  Inverted = false
  LineAngle = 0
  LockPosition = false
  MeasureType = 1
  OverTolerance = 0
  References2D = -> [View004]
  Rotation = 0
  ScaleType = 0
  ShowUnits = false
  TheoreticalExact = false
  Type = 4
  UnderTolerance = 0
  UseActualArea = true
  X = -52.9982
  Y = 22.0252
FEATURE [TechDraw::DrawPage] Page002  label="enclosure front view"
  KeepUpdated = true
  NextBalloonIndex = 1
  ProjectionType = 0
  Template = -> Template002
  Views = -> [View003,Dimension026,Dimension027,Dimension028,Dimension029,Dimension030,Dimension031,Dimension032,Dimension033,Dimension034,Dimension035,Annotation,Annotation005,View004,Dimension047]
FEATURE [TechDraw::DrawViewDimension] Dimension050
  AngleOverride = false
  Arbitrary = false
  ArbitraryTolerances = false
  BoxCorners = (2) [(-123.75,-48.75,0),(123.75,48.75,0)]
  EqualTolerance = true
  ExtensionAngle = 0
  FormatSpec = %.2w
  FormatSpecOverTolerance = %+.2w
  FormatSpecUnderTolerance = %+.2w
  Inverted = false
  LineAngle = 0
  LockPosition = false
  MeasureType = 1
  OverTolerance = 0
  References2D = -> [View002]
  Rotation = 0
  ScaleType = 0
  ShowUnits = false
  TheoreticalExact = false
  Type = 1
  UnderTolerance = 0
  UseActualArea = true
  X = 25.0727
  Y = -57.0904
FEATURE [TechDraw::DrawViewDimension] Dimension051
  AngleOverride = false
  Arbitrary = false
  ArbitraryTolerances = false
  BoxCorners = (2) [(-123.75,-48.75,0),(123.75,48.75,0)]
  EqualTolerance = true
  ExtensionAngle = 0
  FormatSpec = %.2w
  FormatSpecOverTolerance = %+.2w
  FormatSpecUnderTolerance = %+.2w
  Inverted = false
  LineAngle = 0
  LockPosition = false
  MeasureType = 1
  OverTolerance = 0
  References2D = -> [View002]
  Rotation = 0
  ScaleType = 0
  ShowUnits = false
  TheoreticalExact = false
  Type = 0
  UnderTolerance = 0
  UseActualArea = true
  X = -4.80314
  Y = 29.375
FEATURE [TechDraw::DrawViewDimension] Dimension052
  AngleOverride = false
  Arbitrary = false
  ArbitraryTolerances = false
  BoxCorners = (2) [(-123.75,-48.75,-1e-07),(123.75,48.75,1e-07)]
  EqualTolerance = true
  ExtensionAngle = 0
  FormatSpec = %.2w
  FormatSpecOverTolerance = %+.2w
  FormatSpecUnderTolerance = %+.2w
  Inverted = false
  LineAngle = 0
  LockPosition = false
  MeasureType = 1
  OverTolerance = 0
  References2D = -> [View002]
  Rotation = 0
  ScaleType = 0
  ShowUnits = false
  TheoreticalExact = false
  Type = 0
  UnderTolerance = 0
  UseActualArea = true
  X = -22.1095
  Y = -32.0647
FEATURE [TechDraw::DrawViewDimension] Dimension053
  AngleOverride = false
  Arbitrary = false
  ArbitraryTolerances = false
  BoxCorners = (2) [(-123.75,-48.75,-1e-07),(123.75,48.75,1e-07)]
  EqualTolerance = true
  ExtensionAngle = 0
  FormatSpec = %.2w
  FormatSpecOverTolerance = %+.2w
  FormatSpecUnderTolerance = %+.2w
  Inverted = false
  LineAngle = 0
  LockPosition = false
  MeasureType = 1
  OverTolerance = 0
  References2D = -> [View002]
  Rotation = 0
  ScaleType = 0
  ShowUnits = false
  TheoreticalExact = false
  Type = 0
  UnderTolerance = 0
  UseActualArea = true
  X = 44.7383
  Y = -1.04452
FEATURE [TechDraw::DrawViewDimension] Dimension054
  AngleOverride = false
  Arbitrary = false
  ArbitraryTolerances = false
  BoxCorners = (2) [(-123.75,-48.75,0),(123.75,48.75,0)]
  EqualTolerance = true
  ExtensionAngle = 0
  FormatSpec = %.2w
  FormatSpecOverTolerance = %+.2w
  FormatSpecUnderTolerance = %+.2w
  Inverted = false
  LineAngle = 0
  LockPosition = false
  MeasureType = 1
  OverTolerance = 0
  References2D = -> [View002]
  Rotation = 0
  ScaleType = 0
  ShowUnits = false
  TheoreticalExact = false
  Type = 1
  UnderTolerance = 0
  UseActualArea = true
  X = -12.124
  Y = 19.4224
FEATURE [TechDraw::DrawViewDimension] Dimension055
  AngleOverride = false
  Arbitrary = false
  ArbitraryTolerances = false
  BoxCorners = (2) [(-123.75,-48.75,0),(123.75,48.75,0)]
  EqualTolerance = true
  ExtensionAngle = 0
  FormatSpec = R%.2w
  FormatSpecOverTolerance = %+.2w
  FormatSpecUnderTolerance = %+.2w
  Inverted = false
  LineAngle = 0
  LockPosition = false
  MeasureType = 1
  OverTolerance = 0
  References2D = -> [View002]
  Rotation = 0
  ScaleType = 0
  ShowUnits = false
  TheoreticalExact = false
  Type = 4
  UnderTolerance = 0
  UseActualArea = true
  X = 19.9872
  Y = 24.3044
FEATURE [TechDraw::DrawPage] Page  label="enclosure back view"
  KeepUpdated = true
  NextBalloonIndex = 1
  ProjectionType = 0
  Template = -> Template
  Views = -> [View002,Dimension041,Dimension042,Dimension043,Dimension044,Dimension045,Dimension046,Annotation006,Dimension050,Dimension051,Dimension052,Dimension053,Dimension054,Dimension055]
FEATURE [App::DocumentObjectGroup] Group  label="Drawings"
  Group = -> [Page002,Page,Page001,Page003,Body_cs,Body_cs001,Annotation001,Annotation002,Annotation003,Annotation004]
FEATURE [Mesh::Feature] Mesh  label=" "
FEATURE [Sketcher::SketchObject] Sketch020
  ArcFitTolerance = 1e-06
  AttachmentSupport = -> [Mesh]
  ExternalTypes = [0]
  FullyConstrained = true
  MakeInternals = false
  MapMode = 2
  _ExternalGeoVersion = 1
  sketch-geometry (1):
    g0: Circle CenterX=-35 CenterY=0 CenterZ=0 NormalX=0 NormalY=0 NormalZ=1 AngleXU=0 Radius=40
  constraints (3):
    c: PointOnObject(g0,g-1)
    c: DistanceX(g0,g-1) = 35
    c: Diameter(g0) = 80
